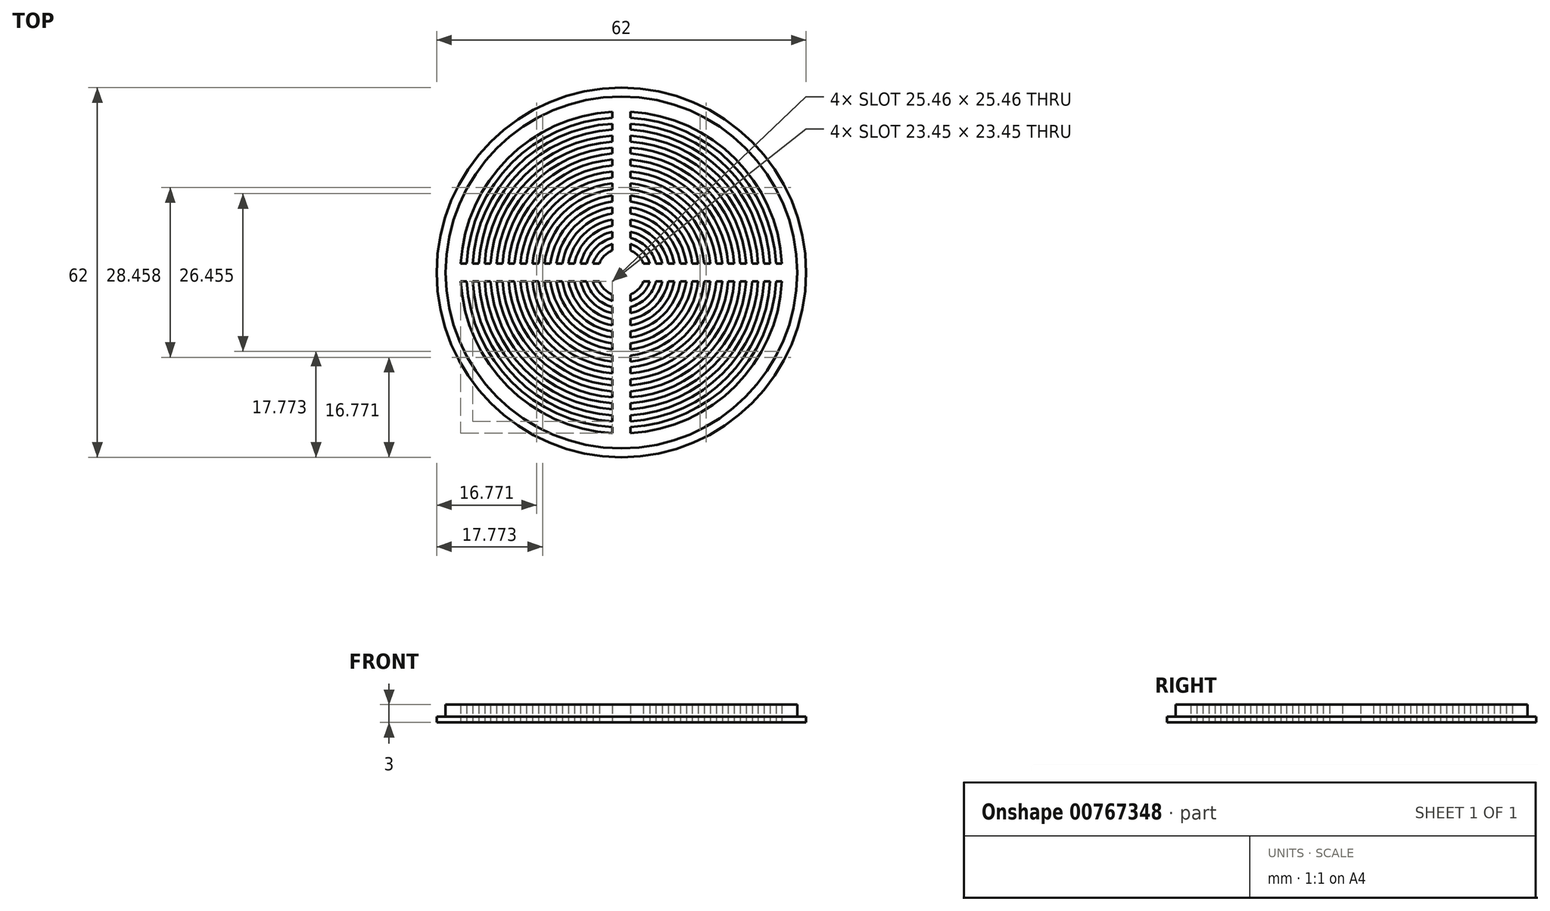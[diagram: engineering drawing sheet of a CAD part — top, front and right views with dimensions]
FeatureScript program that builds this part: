
annotation { "Feature Type Name" : "Feature", "Feature Type Description" : "" }
export const myFeature = defineFeature(function(context is Context, id is Id, definition is map)
    precondition{}
    {
        {
            var Q0;
            Q0=qCreatedBy(makeId("Top.planeOp"),FACE);
            var sketch = newSketch(context, id + "F0", { "sketchPlane" : qUnion([Q0])});
            skPoint(sketch, "E0.middle", {"position": v(0, 0) * mm});
            skCircle(sketch, "E1", {"center": v(0, 0) * mm, "radius": 29.5 * mm});
            skCircle(sketch, "E2", {"center": v(0, 0) * mm, "radius": 27 * mm});
            skCircle(sketch, "E3", {"center": v(0, 0) * mm, "radius": 26 * mm});
            skCircle(sketch, "E4", {"center": v(0, 0) * mm, "radius": 25 * mm});
            skCircle(sketch, "E5", {"center": v(0, 0) * mm, "radius": 24 * mm});
            skCircle(sketch, "E6", {"center": v(0, 0) * mm, "radius": 23 * mm});
            skCircle(sketch, "E7", {"center": v(0, 0) * mm, "radius": 22 * mm});
            skCircle(sketch, "E8", {"center": v(0, 0) * mm, "radius": 21 * mm});
            skCircle(sketch, "E9", {"center": v(0, 0) * mm, "radius": 20 * mm});
            skCircle(sketch, "E10", {"center": v(0, 0) * mm, "radius": 19 * mm});
            skCircle(sketch, "E11", {"center": v(0, 0) * mm, "radius": 18 * mm});
            skCircle(sketch, "E12", {"center": v(0, 0) * mm, "radius": 17 * mm});
            skCircle(sketch, "E13", {"center": v(0, 0) * mm, "radius": 16 * mm});
            skCircle(sketch, "E14", {"center": v(0, 0) * mm, "radius": 15 * mm});
            skCircle(sketch, "E15", {"center": v(0, 0) * mm, "radius": 14 * mm});
            skCircle(sketch, "E16", {"center": v(0, 0) * mm, "radius": 13 * mm});
            skCircle(sketch, "E17", {"center": v(0, 0) * mm, "radius": 12 * mm});
            skCircle(sketch, "E18", {"center": v(0, 0) * mm, "radius": 11 * mm});
            skCircle(sketch, "E19", {"center": v(0, 0) * mm, "radius": 10 * mm});
            skCircle(sketch, "E20", {"center": v(0, 0) * mm, "radius": 9 * mm});
            skCircle(sketch, "E21", {"center": v(0, 0) * mm, "radius": 8 * mm});
            skCircle(sketch, "E22", {"center": v(0, 0) * mm, "radius": 7 * mm});
            skCircle(sketch, "E23", {"center": v(0, 0) * mm, "radius": 6 * mm});
            skCircle(sketch, "E24", {"center": v(0, 0) * mm, "radius": 5 * mm});
            skCircle(sketch, "E25", {"center": v(0, 0) * mm, "radius": 4 * mm});
            skCircle(sketch, "E26", {"center": v(0, 0) * mm, "radius": 3 * mm});
            skCircle(sketch, "E27", {"center": v(0, 0) * mm, "radius": 2 * mm});
            skCircle(sketch, "E28", {"center": v(0, 0) * mm, "radius": 1 * mm});
            skLineSegment(sketch, "E29.bottom", {"start": v(-1.5, 32.48) * mm, "end": v(1.5, 32.48) * mm});
            skLineSegment(sketch, "E29.top", {"start": v(-1.5, -32.48) * mm, "end": v(1.5, -32.48) * mm});
            skLineSegment(sketch, "E29.left", {"start": v(-1.5, 32.48) * mm, "end": v(-1.5, -32.48) * mm});
            skLineSegment(sketch, "E29.right", {"start": v(1.5, 32.48) * mm, "end": v(1.5, -32.48) * mm});
            skLineSegment(sketch, "E30.bottom", {"start": v(36.63, -1.5) * mm, "end": v(-36.63, -1.5) * mm});
            skLineSegment(sketch, "E30.top", {"start": v(36.63, 1.5) * mm, "end": v(-36.63, 1.5) * mm});
            skLineSegment(sketch, "E30.left", {"start": v(36.63, -1.5) * mm, "end": v(36.63, 1.5) * mm});
            skLineSegment(sketch, "E30.right", {"start": v(-36.63, -1.5) * mm, "end": v(-36.63, 1.5) * mm});
            skCircle(sketch, "E31", {"center": v(0, 0) * mm, "radius": 31 * mm});
            skSolve(sketch);
        }
        {
            var Q0;
            {var subQ0=sQuery(id+"F0.wireOp",EDGE,"E30.top");var subQ1=sQuery(id+"F0.wireOp",EDGE,"E10");var subQ2=makeQuery(id+"F0.imprint","INTERSECT",VERTEX,{"disambiguationData":[OD(1.0)],"derivedFrom":[subQ1,subQ0]});Q0=makeQuery(id+"F0.imprint","IMPRINT",FACE,{"disambiguationData":[TD([[makeQuery(id+"F0.imprint","IMPRINT",EDGE,{"disambiguationData":[TD([[subQ2,-1.0]])],"derivedFrom":subQ1}),1.0]])]});}
            var Q1;
            {var subQ0=sQuery(id+"F0.wireOp",EDGE,"E30.top");var subQ1=sQuery(id+"F0.wireOp",EDGE,"E16");var subQ2=makeQuery(id+"F0.imprint","INTERSECT",VERTEX,{"disambiguationData":[OD(1.0)],"derivedFrom":[subQ1,subQ0]});Q1=makeQuery(id+"F0.imprint","IMPRINT",FACE,{"disambiguationData":[TD([[makeQuery(id+"F0.imprint","IMPRINT",EDGE,{"disambiguationData":[TD([[subQ2,-1.0]])],"derivedFrom":subQ1}),1.0]])]});}
            var Q2;
            {var subQ0=sQuery(id+"F0.wireOp",EDGE,"E30.top");var subQ1=sQuery(id+"F0.wireOp",EDGE,"E1");var subQ2=makeQuery(id+"F0.imprint","INTERSECT",VERTEX,{"disambiguationData":[OD(0.0)],"derivedFrom":[subQ1,subQ0]});Q2=makeQuery(id+"F0.imprint","IMPRINT",FACE,{"disambiguationData":[TD([[makeQuery(id+"F0.imprint","IMPRINT",EDGE,{"disambiguationData":[TD([[subQ2,1.0]])],"derivedFrom":subQ1}),1.0]])]});}
            var Q3;
            {var subQ0=sQuery(id+"F0.wireOp",EDGE,"E30.top");var subQ1=sQuery(id+"F0.wireOp",EDGE,"E3");var subQ2=makeQuery(id+"F0.imprint","INTERSECT",VERTEX,{"disambiguationData":[OD(0.0)],"derivedFrom":[subQ1,subQ0]});Q3=makeQuery(id+"F0.imprint","IMPRINT",FACE,{"disambiguationData":[TD([[makeQuery(id+"F0.imprint","IMPRINT",EDGE,{"disambiguationData":[TD([[subQ2,1.0]])],"derivedFrom":subQ1}),1.0]])]});}
            var Q4;
            {var subQ0=sQuery(id+"F0.wireOp",EDGE,"E30.top");var subQ1=sQuery(id+"F0.wireOp",EDGE,"E11");var subQ2=makeQuery(id+"F0.imprint","INTERSECT",VERTEX,{"disambiguationData":[OD(0.0)],"derivedFrom":[subQ1,subQ0]});Q4=makeQuery(id+"F0.imprint","IMPRINT",FACE,{"disambiguationData":[TD([[makeQuery(id+"F0.imprint","IMPRINT",EDGE,{"disambiguationData":[TD([[subQ2,1.0]])],"derivedFrom":subQ1}),1.0]])]});}
            var Q5;
            {var subQ0=sQuery(id+"F0.wireOp",EDGE,"E30.top");var subQ1=sQuery(id+"F0.wireOp",EDGE,"E8");var subQ2=makeQuery(id+"F0.imprint","INTERSECT",VERTEX,{"disambiguationData":[OD(1.0)],"derivedFrom":[subQ1,subQ0]});Q5=makeQuery(id+"F0.imprint","IMPRINT",FACE,{"disambiguationData":[TD([[makeQuery(id+"F0.imprint","IMPRINT",EDGE,{"disambiguationData":[TD([[subQ2,-1.0]])],"derivedFrom":subQ1}),1.0]])]});}
            var Q6;
            {var subQ0=sQuery(id+"F0.wireOp",EDGE,"E30.top");var subQ1=sQuery(id+"F0.wireOp",EDGE,"E2");var subQ2=makeQuery(id+"F0.imprint","INTERSECT",VERTEX,{"disambiguationData":[OD(1.0)],"derivedFrom":[subQ1,subQ0]});Q6=makeQuery(id+"F0.imprint","IMPRINT",FACE,{"disambiguationData":[TD([[makeQuery(id+"F0.imprint","IMPRINT",EDGE,{"disambiguationData":[TD([[subQ2,-1.0]])],"derivedFrom":subQ1}),1.0]])]});}
            var Q7;
            {var subQ3=sQuery(id+"F0.wireOp",EDGE,"E30.top");var subQ6=sQuery(id+"F0.wireOp",EDGE,"E26");var subQ7=makeQuery(id+"F0.imprint","INTERSECT",VERTEX,{"disambiguationData":[OD(1.0)],"derivedFrom":[subQ6,subQ3]});Q7=makeQuery(id+"F0.imprint","IMPRINT",FACE,{"disambiguationData":[TD([[makeQuery(id+"F0.imprint","IMPRINT",EDGE,{"disambiguationData":[TD([[subQ7,-1.0]])],"derivedFrom":subQ6}),1.0]])]});}
            var Q8;
            {var subQ0=sQuery(id+"F0.wireOp",EDGE,"E30.top");var subQ1=sQuery(id+"F0.wireOp",EDGE,"E4");var subQ2=makeQuery(id+"F0.imprint","INTERSECT",VERTEX,{"disambiguationData":[OD(1.0)],"derivedFrom":[subQ1,subQ0]});Q8=makeQuery(id+"F0.imprint","IMPRINT",FACE,{"disambiguationData":[TD([[makeQuery(id+"F0.imprint","IMPRINT",EDGE,{"disambiguationData":[TD([[subQ2,-1.0]])],"derivedFrom":subQ1}),1.0]])]});}
            var Q9;
            {var subQ0=sQuery(id+"F0.wireOp",EDGE,"E30.top");var subQ1=sQuery(id+"F0.wireOp",EDGE,"E6");var subQ2=makeQuery(id+"F0.imprint","INTERSECT",VERTEX,{"disambiguationData":[OD(1.0)],"derivedFrom":[subQ1,subQ0]});Q9=makeQuery(id+"F0.imprint","IMPRINT",FACE,{"disambiguationData":[TD([[makeQuery(id+"F0.imprint","IMPRINT",EDGE,{"disambiguationData":[TD([[subQ2,-1.0]])],"derivedFrom":subQ1}),1.0]])]});}
            var Q10;
            {var subQ0=sQuery(id+"F0.wireOp",EDGE,"E30.top");var subQ1=sQuery(id+"F0.wireOp",EDGE,"E24");var subQ2=makeQuery(id+"F0.imprint","INTERSECT",VERTEX,{"disambiguationData":[OD(0.0)],"derivedFrom":[subQ1,subQ0]});Q10=makeQuery(id+"F0.imprint","IMPRINT",FACE,{"disambiguationData":[TD([[makeQuery(id+"F0.imprint","IMPRINT",EDGE,{"disambiguationData":[TD([[subQ2,1.0]])],"derivedFrom":subQ1}),1.0]])]});}
            var Q11;
            {var subQ0=sQuery(id+"F0.wireOp",EDGE,"E30.top");var subQ1=sQuery(id+"F0.wireOp",EDGE,"E20");var subQ2=makeQuery(id+"F0.imprint","INTERSECT",VERTEX,{"disambiguationData":[OD(1.0)],"derivedFrom":[subQ1,subQ0]});Q11=makeQuery(id+"F0.imprint","IMPRINT",FACE,{"disambiguationData":[TD([[makeQuery(id+"F0.imprint","IMPRINT",EDGE,{"disambiguationData":[TD([[subQ2,-1.0]])],"derivedFrom":subQ1}),1.0]])]});}
            var Q12;
            {var subQ0=sQuery(id+"F0.wireOp",EDGE,"E30.top");var subQ1=sQuery(id+"F0.wireOp",EDGE,"E14");var subQ2=makeQuery(id+"F0.imprint","INTERSECT",VERTEX,{"disambiguationData":[OD(1.0)],"derivedFrom":[subQ1,subQ0]});Q12=makeQuery(id+"F0.imprint","IMPRINT",FACE,{"disambiguationData":[TD([[makeQuery(id+"F0.imprint","IMPRINT",EDGE,{"disambiguationData":[TD([[subQ2,-1.0]])],"derivedFrom":subQ1}),1.0]])]});}
            var Q13;
            {var subQ0=sQuery(id+"F0.wireOp",EDGE,"E30.top");var subQ1=sQuery(id+"F0.wireOp",EDGE,"E12");var subQ2=makeQuery(id+"F0.imprint","INTERSECT",VERTEX,{"disambiguationData":[OD(1.0)],"derivedFrom":[subQ1,subQ0]});Q13=makeQuery(id+"F0.imprint","IMPRINT",FACE,{"disambiguationData":[TD([[makeQuery(id+"F0.imprint","IMPRINT",EDGE,{"disambiguationData":[TD([[subQ2,-1.0]])],"derivedFrom":subQ1}),1.0]])]});}
            var Q14;
            {var subQ0=sQuery(id+"F0.wireOp",EDGE,"E30.top");var subQ1=sQuery(id+"F0.wireOp",EDGE,"E22");var subQ2=makeQuery(id+"F0.imprint","INTERSECT",VERTEX,{"disambiguationData":[OD(1.0)],"derivedFrom":[subQ1,subQ0]});Q14=makeQuery(id+"F0.imprint","IMPRINT",FACE,{"disambiguationData":[TD([[makeQuery(id+"F0.imprint","IMPRINT",EDGE,{"disambiguationData":[TD([[subQ2,-1.0]])],"derivedFrom":subQ1}),1.0]])]});}
            var Q15;
            {var subQ3=sQuery(id+"F0.wireOp",EDGE,"E30.top");var subQ8=sQuery(id+"F0.wireOp",EDGE,"E26");var subQ9=makeQuery(id+"F0.imprint","INTERSECT",VERTEX,{"disambiguationData":[OD(0.0)],"derivedFrom":[subQ8,subQ3]});Q15=makeQuery(id+"F0.imprint","IMPRINT",FACE,{"disambiguationData":[TD([[makeQuery(id+"F0.imprint","IMPRINT",EDGE,{"disambiguationData":[TD([[subQ9,1.0]])],"derivedFrom":subQ8}),1.0]])]});}
            var Q16;
            {var subQ0=sQuery(id+"F0.wireOp",EDGE,"E30.top");var subQ1=sQuery(id+"F0.wireOp",EDGE,"E24");var subQ2=makeQuery(id+"F0.imprint","INTERSECT",VERTEX,{"disambiguationData":[OD(1.0)],"derivedFrom":[subQ1,subQ0]});Q16=makeQuery(id+"F0.imprint","IMPRINT",FACE,{"disambiguationData":[TD([[makeQuery(id+"F0.imprint","IMPRINT",EDGE,{"disambiguationData":[TD([[subQ2,-1.0]])],"derivedFrom":subQ1}),1.0]])]});}
            var Q17;
            {var subQ0=sQuery(id+"F0.wireOp",EDGE,"E30.top");var subQ1=sQuery(id+"F0.wireOp",EDGE,"E18");var subQ2=makeQuery(id+"F0.imprint","INTERSECT",VERTEX,{"disambiguationData":[OD(1.0)],"derivedFrom":[subQ1,subQ0]});Q17=makeQuery(id+"F0.imprint","IMPRINT",FACE,{"disambiguationData":[TD([[makeQuery(id+"F0.imprint","IMPRINT",EDGE,{"disambiguationData":[TD([[subQ2,-1.0]])],"derivedFrom":subQ1}),1.0]])]});}
            var Q18;
            {var subQ0=sQuery(id+"F0.wireOp",EDGE,"E30.top");var subQ1=sQuery(id+"F0.wireOp",EDGE,"E13");var subQ2=makeQuery(id+"F0.imprint","INTERSECT",VERTEX,{"disambiguationData":[OD(0.0)],"derivedFrom":[subQ1,subQ0]});Q18=makeQuery(id+"F0.imprint","IMPRINT",FACE,{"disambiguationData":[TD([[makeQuery(id+"F0.imprint","IMPRINT",EDGE,{"disambiguationData":[TD([[subQ2,1.0]])],"derivedFrom":subQ1}),1.0]])]});}
            var Q19;
            {var subQ0=sQuery(id+"F0.wireOp",EDGE,"E30.top");var subQ1=sQuery(id+"F0.wireOp",EDGE,"E25");var subQ2=makeQuery(id+"F0.imprint","INTERSECT",VERTEX,{"disambiguationData":[OD(0.0)],"derivedFrom":[subQ1,subQ0]});Q19=makeQuery(id+"F0.imprint","IMPRINT",FACE,{"disambiguationData":[TD([[makeQuery(id+"F0.imprint","IMPRINT",EDGE,{"disambiguationData":[TD([[subQ2,1.0]])],"derivedFrom":subQ1}),1.0]])]});}
            var Q20;
            {var subQ0=sQuery(id+"F0.wireOp",EDGE,"E30.top");var subQ1=sQuery(id+"F0.wireOp",EDGE,"E20");var subQ2=makeQuery(id+"F0.imprint","INTERSECT",VERTEX,{"disambiguationData":[OD(0.0)],"derivedFrom":[subQ1,subQ0]});Q20=makeQuery(id+"F0.imprint","IMPRINT",FACE,{"disambiguationData":[TD([[makeQuery(id+"F0.imprint","IMPRINT",EDGE,{"disambiguationData":[TD([[subQ2,1.0]])],"derivedFrom":subQ1}),1.0]])]});}
            var Q21;
            {var subQ0=sQuery(id+"F0.wireOp",EDGE,"E30.top");var subQ1=sQuery(id+"F0.wireOp",EDGE,"E17");var subQ2=makeQuery(id+"F0.imprint","INTERSECT",VERTEX,{"disambiguationData":[OD(0.0)],"derivedFrom":[subQ1,subQ0]});Q21=makeQuery(id+"F0.imprint","IMPRINT",FACE,{"disambiguationData":[TD([[makeQuery(id+"F0.imprint","IMPRINT",EDGE,{"disambiguationData":[TD([[subQ2,1.0]])],"derivedFrom":subQ1}),1.0]])]});}
            var Q22;
            {var subQ0=sQuery(id+"F0.wireOp",EDGE,"E30.top");var subQ1=sQuery(id+"F0.wireOp",EDGE,"E10");var subQ2=makeQuery(id+"F0.imprint","INTERSECT",VERTEX,{"disambiguationData":[OD(0.0)],"derivedFrom":[subQ1,subQ0]});Q22=makeQuery(id+"F0.imprint","IMPRINT",FACE,{"disambiguationData":[TD([[makeQuery(id+"F0.imprint","IMPRINT",EDGE,{"disambiguationData":[TD([[subQ2,1.0]])],"derivedFrom":subQ1}),1.0]])]});}
            var Q23;
            {var subQ0=sQuery(id+"F0.wireOp",EDGE,"E30.top");var subQ1=sQuery(id+"F0.wireOp",EDGE,"E22");var subQ2=makeQuery(id+"F0.imprint","INTERSECT",VERTEX,{"disambiguationData":[OD(0.0)],"derivedFrom":[subQ1,subQ0]});Q23=makeQuery(id+"F0.imprint","IMPRINT",FACE,{"disambiguationData":[TD([[makeQuery(id+"F0.imprint","IMPRINT",EDGE,{"disambiguationData":[TD([[subQ2,1.0]])],"derivedFrom":subQ1}),1.0]])]});}
            var Q24;
            {var subQ0=sQuery(id+"F0.wireOp",EDGE,"E30.top");var subQ1=sQuery(id+"F0.wireOp",EDGE,"E12");var subQ2=makeQuery(id+"F0.imprint","INTERSECT",VERTEX,{"disambiguationData":[OD(0.0)],"derivedFrom":[subQ1,subQ0]});Q24=makeQuery(id+"F0.imprint","IMPRINT",FACE,{"disambiguationData":[TD([[makeQuery(id+"F0.imprint","IMPRINT",EDGE,{"disambiguationData":[TD([[subQ2,1.0]])],"derivedFrom":subQ1}),1.0]])]});}
            var Q25;
            {var subQ0=sQuery(id+"F0.wireOp",EDGE,"E30.top");var subQ1=sQuery(id+"F0.wireOp",EDGE,"E23");var subQ2=makeQuery(id+"F0.imprint","INTERSECT",VERTEX,{"disambiguationData":[OD(0.0)],"derivedFrom":[subQ1,subQ0]});Q25=makeQuery(id+"F0.imprint","IMPRINT",FACE,{"disambiguationData":[TD([[makeQuery(id+"F0.imprint","IMPRINT",EDGE,{"disambiguationData":[TD([[subQ2,1.0]])],"derivedFrom":subQ1}),1.0]])]});}
            var Q26;
            {var subQ0=sQuery(id+"F0.wireOp",EDGE,"E30.top");var subQ1=sQuery(id+"F0.wireOp",EDGE,"E19");var subQ2=makeQuery(id+"F0.imprint","INTERSECT",VERTEX,{"disambiguationData":[OD(0.0)],"derivedFrom":[subQ1,subQ0]});Q26=makeQuery(id+"F0.imprint","IMPRINT",FACE,{"disambiguationData":[TD([[makeQuery(id+"F0.imprint","IMPRINT",EDGE,{"disambiguationData":[TD([[subQ2,1.0]])],"derivedFrom":subQ1}),1.0]])]});}
            var Q27;
            {var subQ0=sQuery(id+"F0.wireOp",EDGE,"E30.top");var subQ1=sQuery(id+"F0.wireOp",EDGE,"E21");var subQ2=makeQuery(id+"F0.imprint","INTERSECT",VERTEX,{"disambiguationData":[OD(0.0)],"derivedFrom":[subQ1,subQ0]});Q27=makeQuery(id+"F0.imprint","IMPRINT",FACE,{"disambiguationData":[TD([[makeQuery(id+"F0.imprint","IMPRINT",EDGE,{"disambiguationData":[TD([[subQ2,1.0]])],"derivedFrom":subQ1}),1.0]])]});}
            var Q28;
            {var subQ0=sQuery(id+"F0.wireOp",EDGE,"E30.top");var subQ1=sQuery(id+"F0.wireOp",EDGE,"E7");var subQ2=makeQuery(id+"F0.imprint","INTERSECT",VERTEX,{"disambiguationData":[OD(0.0)],"derivedFrom":[subQ1,subQ0]});Q28=makeQuery(id+"F0.imprint","IMPRINT",FACE,{"disambiguationData":[TD([[makeQuery(id+"F0.imprint","IMPRINT",EDGE,{"disambiguationData":[TD([[subQ2,1.0]])],"derivedFrom":subQ1}),1.0]])]});}
            var Q29;
            {var subQ0=sQuery(id+"F0.wireOp",EDGE,"E30.top");var subQ1=sQuery(id+"F0.wireOp",EDGE,"E9");var subQ2=makeQuery(id+"F0.imprint","INTERSECT",VERTEX,{"disambiguationData":[OD(0.0)],"derivedFrom":[subQ1,subQ0]});Q29=makeQuery(id+"F0.imprint","IMPRINT",FACE,{"disambiguationData":[TD([[makeQuery(id+"F0.imprint","IMPRINT",EDGE,{"disambiguationData":[TD([[subQ2,1.0]])],"derivedFrom":subQ1}),1.0]])]});}
            var Q30;
            {var subQ0=sQuery(id+"F0.wireOp",EDGE,"E30.top");var subQ1=sQuery(id+"F0.wireOp",EDGE,"E18");var subQ2=makeQuery(id+"F0.imprint","INTERSECT",VERTEX,{"disambiguationData":[OD(0.0)],"derivedFrom":[subQ1,subQ0]});Q30=makeQuery(id+"F0.imprint","IMPRINT",FACE,{"disambiguationData":[TD([[makeQuery(id+"F0.imprint","IMPRINT",EDGE,{"disambiguationData":[TD([[subQ2,1.0]])],"derivedFrom":subQ1}),1.0]])]});}
            var Q31;
            {var subQ0=sQuery(id+"F0.wireOp",EDGE,"E30.top");var subQ1=sQuery(id+"F0.wireOp",EDGE,"E15");var subQ2=makeQuery(id+"F0.imprint","INTERSECT",VERTEX,{"disambiguationData":[OD(0.0)],"derivedFrom":[subQ1,subQ0]});Q31=makeQuery(id+"F0.imprint","IMPRINT",FACE,{"disambiguationData":[TD([[makeQuery(id+"F0.imprint","IMPRINT",EDGE,{"disambiguationData":[TD([[subQ2,1.0]])],"derivedFrom":subQ1}),1.0]])]});}
            var Q32;
            {var subQ0=sQuery(id+"F0.wireOp",EDGE,"E30.top");var subQ1=sQuery(id+"F0.wireOp",EDGE,"E5");var subQ2=makeQuery(id+"F0.imprint","INTERSECT",VERTEX,{"disambiguationData":[OD(0.0)],"derivedFrom":[subQ1,subQ0]});Q32=makeQuery(id+"F0.imprint","IMPRINT",FACE,{"disambiguationData":[TD([[makeQuery(id+"F0.imprint","IMPRINT",EDGE,{"disambiguationData":[TD([[subQ2,1.0]])],"derivedFrom":subQ1}),1.0]])]});}
            var Q33;
            {var subQ0=sQuery(id+"F0.wireOp",EDGE,"E30.top");var subQ1=sQuery(id+"F0.wireOp",EDGE,"E8");var subQ2=makeQuery(id+"F0.imprint","INTERSECT",VERTEX,{"disambiguationData":[OD(0.0)],"derivedFrom":[subQ1,subQ0]});Q33=makeQuery(id+"F0.imprint","IMPRINT",FACE,{"disambiguationData":[TD([[makeQuery(id+"F0.imprint","IMPRINT",EDGE,{"disambiguationData":[TD([[subQ2,1.0]])],"derivedFrom":subQ1}),1.0]])]});}
            var Q34;
            {var subQ0=sQuery(id+"F0.wireOp",EDGE,"E30.top");var subQ1=sQuery(id+"F0.wireOp",EDGE,"E4");var subQ2=makeQuery(id+"F0.imprint","INTERSECT",VERTEX,{"disambiguationData":[OD(0.0)],"derivedFrom":[subQ1,subQ0]});Q34=makeQuery(id+"F0.imprint","IMPRINT",FACE,{"disambiguationData":[TD([[makeQuery(id+"F0.imprint","IMPRINT",EDGE,{"disambiguationData":[TD([[subQ2,1.0]])],"derivedFrom":subQ1}),1.0]])]});}
            var Q35;
            {var subQ0=sQuery(id+"F0.wireOp",EDGE,"E30.top");var subQ1=sQuery(id+"F0.wireOp",EDGE,"E6");var subQ2=makeQuery(id+"F0.imprint","INTERSECT",VERTEX,{"disambiguationData":[OD(0.0)],"derivedFrom":[subQ1,subQ0]});Q35=makeQuery(id+"F0.imprint","IMPRINT",FACE,{"disambiguationData":[TD([[makeQuery(id+"F0.imprint","IMPRINT",EDGE,{"disambiguationData":[TD([[subQ2,1.0]])],"derivedFrom":subQ1}),1.0]])]});}
            var Q36;
            {var subQ0=sQuery(id+"F0.wireOp",EDGE,"E30.top");var subQ1=sQuery(id+"F0.wireOp",EDGE,"E2");var subQ2=makeQuery(id+"F0.imprint","INTERSECT",VERTEX,{"disambiguationData":[OD(0.0)],"derivedFrom":[subQ1,subQ0]});Q36=makeQuery(id+"F0.imprint","IMPRINT",FACE,{"disambiguationData":[TD([[makeQuery(id+"F0.imprint","IMPRINT",EDGE,{"disambiguationData":[TD([[subQ2,1.0]])],"derivedFrom":subQ1}),1.0]])]});}
            var Q37;
            {var subQ0=sQuery(id+"F0.wireOp",EDGE,"E30.top");var subQ1=sQuery(id+"F0.wireOp",EDGE,"E14");var subQ2=makeQuery(id+"F0.imprint","INTERSECT",VERTEX,{"disambiguationData":[OD(0.0)],"derivedFrom":[subQ1,subQ0]});Q37=makeQuery(id+"F0.imprint","IMPRINT",FACE,{"disambiguationData":[TD([[makeQuery(id+"F0.imprint","IMPRINT",EDGE,{"disambiguationData":[TD([[subQ2,1.0]])],"derivedFrom":subQ1}),1.0]])]});}
            var Q38;
            {var subQ0=sQuery(id+"F0.wireOp",EDGE,"E30.top");var subQ1=sQuery(id+"F0.wireOp",EDGE,"E16");var subQ2=makeQuery(id+"F0.imprint","INTERSECT",VERTEX,{"disambiguationData":[OD(0.0)],"derivedFrom":[subQ1,subQ0]});Q38=makeQuery(id+"F0.imprint","IMPRINT",FACE,{"disambiguationData":[TD([[makeQuery(id+"F0.imprint","IMPRINT",EDGE,{"disambiguationData":[TD([[subQ2,1.0]])],"derivedFrom":subQ1}),1.0]])]});}
            var Q39;
            {var subQ0=sQuery(id+"F0.wireOp",EDGE,"E30.top");var subQ1=sQuery(id+"F0.wireOp",EDGE,"E9");var subQ2=makeQuery(id+"F0.imprint","INTERSECT",VERTEX,{"disambiguationData":[OD(1.0)],"derivedFrom":[subQ1,subQ0]});Q39=makeQuery(id+"F0.imprint","IMPRINT",FACE,{"disambiguationData":[TD([[makeQuery(id+"F0.imprint","IMPRINT",EDGE,{"disambiguationData":[TD([[subQ2,-1.0]])],"derivedFrom":subQ1}),1.0]])]});}
            var Q40;
            {var subQ0=sQuery(id+"F0.wireOp",EDGE,"E30.top");var subQ1=sQuery(id+"F0.wireOp",EDGE,"E7");var subQ2=makeQuery(id+"F0.imprint","INTERSECT",VERTEX,{"disambiguationData":[OD(1.0)],"derivedFrom":[subQ1,subQ0]});Q40=makeQuery(id+"F0.imprint","IMPRINT",FACE,{"disambiguationData":[TD([[makeQuery(id+"F0.imprint","IMPRINT",EDGE,{"disambiguationData":[TD([[subQ2,-1.0]])],"derivedFrom":subQ1}),1.0]])]});}
            var Q41;
            {var subQ0=sQuery(id+"F0.wireOp",EDGE,"E30.top");var subQ1=sQuery(id+"F0.wireOp",EDGE,"E5");var subQ2=makeQuery(id+"F0.imprint","INTERSECT",VERTEX,{"disambiguationData":[OD(1.0)],"derivedFrom":[subQ1,subQ0]});Q41=makeQuery(id+"F0.imprint","IMPRINT",FACE,{"disambiguationData":[TD([[makeQuery(id+"F0.imprint","IMPRINT",EDGE,{"disambiguationData":[TD([[subQ2,-1.0]])],"derivedFrom":subQ1}),1.0]])]});}
            var Q42;
            {var subQ0=sQuery(id+"F0.wireOp",EDGE,"E30.top");var subQ1=sQuery(id+"F0.wireOp",EDGE,"E3");var subQ2=makeQuery(id+"F0.imprint","INTERSECT",VERTEX,{"disambiguationData":[OD(1.0)],"derivedFrom":[subQ1,subQ0]});Q42=makeQuery(id+"F0.imprint","IMPRINT",FACE,{"disambiguationData":[TD([[makeQuery(id+"F0.imprint","IMPRINT",EDGE,{"disambiguationData":[TD([[subQ2,-1.0]])],"derivedFrom":subQ1}),1.0]])]});}
            var Q43;
            {var subQ0=sQuery(id+"F0.wireOp",EDGE,"E30.top");var subQ1=sQuery(id+"F0.wireOp",EDGE,"E17");var subQ2=makeQuery(id+"F0.imprint","INTERSECT",VERTEX,{"disambiguationData":[OD(1.0)],"derivedFrom":[subQ1,subQ0]});Q43=makeQuery(id+"F0.imprint","IMPRINT",FACE,{"disambiguationData":[TD([[makeQuery(id+"F0.imprint","IMPRINT",EDGE,{"disambiguationData":[TD([[subQ2,-1.0]])],"derivedFrom":subQ1}),1.0]])]});}
            var Q44;
            {var subQ0=sQuery(id+"F0.wireOp",EDGE,"E30.top");var subQ1=sQuery(id+"F0.wireOp",EDGE,"E15");var subQ2=makeQuery(id+"F0.imprint","INTERSECT",VERTEX,{"disambiguationData":[OD(1.0)],"derivedFrom":[subQ1,subQ0]});Q44=makeQuery(id+"F0.imprint","IMPRINT",FACE,{"disambiguationData":[TD([[makeQuery(id+"F0.imprint","IMPRINT",EDGE,{"disambiguationData":[TD([[subQ2,-1.0]])],"derivedFrom":subQ1}),1.0]])]});}
            var Q45;
            {var subQ0=sQuery(id+"F0.wireOp",EDGE,"E30.top");var subQ1=sQuery(id+"F0.wireOp",EDGE,"E13");var subQ2=makeQuery(id+"F0.imprint","INTERSECT",VERTEX,{"disambiguationData":[OD(1.0)],"derivedFrom":[subQ1,subQ0]});Q45=makeQuery(id+"F0.imprint","IMPRINT",FACE,{"disambiguationData":[TD([[makeQuery(id+"F0.imprint","IMPRINT",EDGE,{"disambiguationData":[TD([[subQ2,-1.0]])],"derivedFrom":subQ1}),1.0]])]});}
            var Q46;
            {var subQ0=sQuery(id+"F0.wireOp",EDGE,"E30.top");var subQ1=sQuery(id+"F0.wireOp",EDGE,"E11");var subQ2=makeQuery(id+"F0.imprint","INTERSECT",VERTEX,{"disambiguationData":[OD(1.0)],"derivedFrom":[subQ1,subQ0]});Q46=makeQuery(id+"F0.imprint","IMPRINT",FACE,{"disambiguationData":[TD([[makeQuery(id+"F0.imprint","IMPRINT",EDGE,{"disambiguationData":[TD([[subQ2,-1.0]])],"derivedFrom":subQ1}),1.0]])]});}
            var Q47;
            {var subQ0=sQuery(id+"F0.wireOp",EDGE,"E30.top");var subQ1=sQuery(id+"F0.wireOp",EDGE,"E25");var subQ2=makeQuery(id+"F0.imprint","INTERSECT",VERTEX,{"disambiguationData":[OD(1.0)],"derivedFrom":[subQ1,subQ0]});Q47=makeQuery(id+"F0.imprint","IMPRINT",FACE,{"disambiguationData":[TD([[makeQuery(id+"F0.imprint","IMPRINT",EDGE,{"disambiguationData":[TD([[subQ2,-1.0]])],"derivedFrom":subQ1}),1.0]])]});}
            var Q48;
            {var subQ0=sQuery(id+"F0.wireOp",EDGE,"E30.top");var subQ1=sQuery(id+"F0.wireOp",EDGE,"E23");var subQ2=makeQuery(id+"F0.imprint","INTERSECT",VERTEX,{"disambiguationData":[OD(1.0)],"derivedFrom":[subQ1,subQ0]});Q48=makeQuery(id+"F0.imprint","IMPRINT",FACE,{"disambiguationData":[TD([[makeQuery(id+"F0.imprint","IMPRINT",EDGE,{"disambiguationData":[TD([[subQ2,-1.0]])],"derivedFrom":subQ1}),1.0]])]});}
            var Q49;
            {var subQ0=sQuery(id+"F0.wireOp",EDGE,"E30.top");var subQ1=sQuery(id+"F0.wireOp",EDGE,"E21");var subQ2=makeQuery(id+"F0.imprint","INTERSECT",VERTEX,{"disambiguationData":[OD(1.0)],"derivedFrom":[subQ1,subQ0]});Q49=makeQuery(id+"F0.imprint","IMPRINT",FACE,{"disambiguationData":[TD([[makeQuery(id+"F0.imprint","IMPRINT",EDGE,{"disambiguationData":[TD([[subQ2,-1.0]])],"derivedFrom":subQ1}),1.0]])]});}
            var Q50;
            {var subQ0=sQuery(id+"F0.wireOp",EDGE,"E30.top");var subQ1=sQuery(id+"F0.wireOp",EDGE,"E19");var subQ2=makeQuery(id+"F0.imprint","INTERSECT",VERTEX,{"disambiguationData":[OD(1.0)],"derivedFrom":[subQ1,subQ0]});Q50=makeQuery(id+"F0.imprint","IMPRINT",FACE,{"disambiguationData":[TD([[makeQuery(id+"F0.imprint","IMPRINT",EDGE,{"disambiguationData":[TD([[subQ2,-1.0]])],"derivedFrom":subQ1}),1.0]])]});}
            var Q51;
            {var subQ0=sQuery(id+"F0.wireOp",EDGE,"E30.top");var subQ1=sQuery(id+"F0.wireOp",EDGE,"E1");var subQ2=makeQuery(id+"F0.imprint","INTERSECT",VERTEX,{"disambiguationData":[OD(1.0)],"derivedFrom":[subQ1,subQ0]});Q51=makeQuery(id+"F0.imprint","IMPRINT",FACE,{"disambiguationData":[TD([[makeQuery(id+"F0.imprint","IMPRINT",EDGE,{"disambiguationData":[TD([[subQ2,-1.0]])],"derivedFrom":subQ1}),1.0]])]});}
            var Q52;
            Q52=makeQuery(id+"F0.imprint","IMPRINT",FACE,{"disambiguationData":[TD([[makeQuery(id+"F0.imprint","IMPRINT",EDGE,{"derivedFrom":sQuery(id+"F0.wireOp",EDGE,"E28")}),-1.0]])]});
            var Q53;
            {var subQ0=sQuery(id+"F0.wireOp",EDGE,"E30.top");var subQ1=sQuery(id+"F0.wireOp",EDGE,"E27");var subQ2=makeQuery(id+"F0.imprint","INTERSECT",VERTEX,{"disambiguationData":[OD(0.0)],"derivedFrom":[subQ1,subQ0]});Q53=makeQuery(id+"F0.imprint","IMPRINT",FACE,{"disambiguationData":[TD([[makeQuery(id+"F0.imprint","IMPRINT",EDGE,{"disambiguationData":[TD([[subQ2,1.0]])],"derivedFrom":subQ1}),-1.0]])]});}
            var Q54;
            {var subQ0=sQuery(id+"F0.wireOp",EDGE,"E29.right");var subQ1=sQuery(id+"F0.wireOp",EDGE,"E27");var subQ2=makeQuery(id+"F0.imprint","INTERSECT",VERTEX,{"disambiguationData":[OD(0.0)],"derivedFrom":[subQ1,subQ0]});Q54=makeQuery(id+"F0.imprint","IMPRINT",FACE,{"disambiguationData":[TD([[makeQuery(id+"F0.imprint","IMPRINT",EDGE,{"disambiguationData":[TD([[subQ2,1.0]])],"derivedFrom":subQ1}),1.0]])]});}
            var Q55;
            {var subQ0=sQuery(id+"F0.wireOp",EDGE,"E30.bottom");var subQ1=sQuery(id+"F0.wireOp",EDGE,"E27");var subQ2=makeQuery(id+"F0.imprint","INTERSECT",VERTEX,{"disambiguationData":[OD(0.0)],"derivedFrom":[subQ1,subQ0]});Q55=makeQuery(id+"F0.imprint","IMPRINT",FACE,{"disambiguationData":[TD([[makeQuery(id+"F0.imprint","IMPRINT",EDGE,{"disambiguationData":[TD([[subQ2,-1.0]])],"derivedFrom":subQ1}),1.0]])]});}
            var Q56;
            {var subQ0=sQuery(id+"F0.wireOp",EDGE,"E29.left");var subQ1=sQuery(id+"F0.wireOp",EDGE,"E27");var subQ2=makeQuery(id+"F0.imprint","INTERSECT",VERTEX,{"disambiguationData":[OD(0.0)],"derivedFrom":[subQ1,subQ0]});Q56=makeQuery(id+"F0.imprint","IMPRINT",FACE,{"disambiguationData":[TD([[makeQuery(id+"F0.imprint","IMPRINT",EDGE,{"disambiguationData":[TD([[subQ2,-1.0]])],"derivedFrom":subQ1}),1.0]])]});}
            var Q57;
            {var subQ0=sQuery(id+"F0.wireOp",EDGE,"E30.top");var subQ1=sQuery(id+"F0.wireOp",EDGE,"E27");var subQ2=makeQuery(id+"F0.imprint","INTERSECT",VERTEX,{"disambiguationData":[OD(0.0)],"derivedFrom":[subQ1,subQ0]});Q57=makeQuery(id+"F0.imprint","IMPRINT",FACE,{"disambiguationData":[TD([[makeQuery(id+"F0.imprint","IMPRINT",EDGE,{"disambiguationData":[TD([[subQ2,-1.0]])],"derivedFrom":subQ1}),1.0]])]});}
            var Q58;
            {var subQ0=sQuery(id+"F0.wireOp",EDGE,"E29.left");var subQ1=sQuery(id+"F0.wireOp",EDGE,"E27");var subQ2=makeQuery(id+"F0.imprint","INTERSECT",VERTEX,{"disambiguationData":[OD(1.0)],"derivedFrom":[subQ1,subQ0]});Q58=makeQuery(id+"F0.imprint","IMPRINT",FACE,{"disambiguationData":[TD([[makeQuery(id+"F0.imprint","IMPRINT",EDGE,{"disambiguationData":[TD([[subQ2,-1.0]])],"derivedFrom":subQ1}),-1.0]])]});}
            var Q59;
            {var subQ0=sQuery(id+"F0.wireOp",EDGE,"E30.top");var subQ1=sQuery(id+"F0.wireOp",EDGE,"E27");var subQ2=makeQuery(id+"F0.imprint","INTERSECT",VERTEX,{"disambiguationData":[OD(1.0)],"derivedFrom":[subQ1,subQ0]});Q59=makeQuery(id+"F0.imprint","IMPRINT",FACE,{"disambiguationData":[TD([[makeQuery(id+"F0.imprint","IMPRINT",EDGE,{"disambiguationData":[TD([[subQ2,-1.0]])],"derivedFrom":subQ1}),-1.0]])]});}
            var Q60;
            {var subQ0=sQuery(id+"F0.wireOp",EDGE,"E30.bottom");var subQ1=sQuery(id+"F0.wireOp",EDGE,"E27");var subQ2=makeQuery(id+"F0.imprint","INTERSECT",VERTEX,{"disambiguationData":[OD(1.0)],"derivedFrom":[subQ1,subQ0]});Q60=makeQuery(id+"F0.imprint","IMPRINT",FACE,{"disambiguationData":[TD([[makeQuery(id+"F0.imprint","IMPRINT",EDGE,{"disambiguationData":[TD([[subQ2,-1.0]])],"derivedFrom":subQ1}),-1.0]])]});}
            var Q61;
            Q61=makeQuery(id+"F0.imprint","IMPRINT",FACE,{"disambiguationData":[TD([[makeQuery(id+"F0.imprint","IMPRINT",EDGE,{"derivedFrom":sQuery(id+"F0.wireOp",EDGE,"E28")}),1.0]])]});
            var Q62;
            {var subQ0=sQuery(id+"F0.wireOp",EDGE,"E29.right");var subQ1=sQuery(id+"F0.wireOp",EDGE,"E20");var subQ2=makeQuery(id+"F0.imprint","INTERSECT",VERTEX,{"disambiguationData":[OD(0.0)],"derivedFrom":[subQ1,subQ0]});Q62=makeQuery(id+"F0.imprint","IMPRINT",FACE,{"disambiguationData":[TD([[makeQuery(id+"F0.imprint","IMPRINT",EDGE,{"disambiguationData":[TD([[subQ2,-1.0]])],"derivedFrom":subQ1}),1.0]])]});}
            var Q63;
            {var subQ0=sQuery(id+"F0.wireOp",EDGE,"E29.left");var subQ1=sQuery(id+"F0.wireOp",EDGE,"E22");var subQ2=makeQuery(id+"F0.imprint","INTERSECT",VERTEX,{"disambiguationData":[OD(1.0)],"derivedFrom":[subQ1,subQ0]});Q63=makeQuery(id+"F0.imprint","IMPRINT",FACE,{"disambiguationData":[TD([[makeQuery(id+"F0.imprint","IMPRINT",EDGE,{"disambiguationData":[TD([[subQ2,-1.0]])],"derivedFrom":subQ1}),1.0]])]});}
            var Q64;
            {var subQ0=sQuery(id+"F0.wireOp",EDGE,"E29.right");var subQ1=sQuery(id+"F0.wireOp",EDGE,"E14");var subQ2=makeQuery(id+"F0.imprint","INTERSECT",VERTEX,{"disambiguationData":[OD(0.0)],"derivedFrom":[subQ1,subQ0]});Q64=makeQuery(id+"F0.imprint","IMPRINT",FACE,{"disambiguationData":[TD([[makeQuery(id+"F0.imprint","IMPRINT",EDGE,{"disambiguationData":[TD([[subQ2,-1.0]])],"derivedFrom":subQ1}),1.0]])]});}
            var Q65;
            {var subQ0=sQuery(id+"F0.wireOp",EDGE,"E29.right");var subQ1=sQuery(id+"F0.wireOp",EDGE,"E24");var subQ2=makeQuery(id+"F0.imprint","INTERSECT",VERTEX,{"disambiguationData":[OD(0.0)],"derivedFrom":[subQ1,subQ0]});Q65=makeQuery(id+"F0.imprint","IMPRINT",FACE,{"disambiguationData":[TD([[makeQuery(id+"F0.imprint","IMPRINT",EDGE,{"disambiguationData":[TD([[subQ2,-1.0]])],"derivedFrom":subQ1}),1.0]])]});}
            var Q66;
            {var subQ0=sQuery(id+"F0.wireOp",EDGE,"E29.left");var subQ1=sQuery(id+"F0.wireOp",EDGE,"E6");var subQ2=makeQuery(id+"F0.imprint","INTERSECT",VERTEX,{"disambiguationData":[OD(1.0)],"derivedFrom":[subQ1,subQ0]});Q66=makeQuery(id+"F0.imprint","IMPRINT",FACE,{"disambiguationData":[TD([[makeQuery(id+"F0.imprint","IMPRINT",EDGE,{"disambiguationData":[TD([[subQ2,-1.0]])],"derivedFrom":subQ1}),1.0]])]});}
            var Q67;
            {var subQ0=sQuery(id+"F0.wireOp",EDGE,"E29.right");var subQ1=sQuery(id+"F0.wireOp",EDGE,"E18");var subQ2=makeQuery(id+"F0.imprint","INTERSECT",VERTEX,{"disambiguationData":[OD(0.0)],"derivedFrom":[subQ1,subQ0]});Q67=makeQuery(id+"F0.imprint","IMPRINT",FACE,{"disambiguationData":[TD([[makeQuery(id+"F0.imprint","IMPRINT",EDGE,{"disambiguationData":[TD([[subQ2,-1.0]])],"derivedFrom":subQ1}),1.0]])]});}
            var Q68;
            {var subQ0=sQuery(id+"F0.wireOp",EDGE,"E29.left");var subQ1=sQuery(id+"F0.wireOp",EDGE,"E4");var subQ2=makeQuery(id+"F0.imprint","INTERSECT",VERTEX,{"disambiguationData":[OD(1.0)],"derivedFrom":[subQ1,subQ0]});Q68=makeQuery(id+"F0.imprint","IMPRINT",FACE,{"disambiguationData":[TD([[makeQuery(id+"F0.imprint","IMPRINT",EDGE,{"disambiguationData":[TD([[subQ2,-1.0]])],"derivedFrom":subQ1}),1.0]])]});}
            var Q69;
            {var subQ0=sQuery(id+"F0.wireOp",EDGE,"E29.left");var subQ1=sQuery(id+"F0.wireOp",EDGE,"E18");var subQ2=makeQuery(id+"F0.imprint","INTERSECT",VERTEX,{"disambiguationData":[OD(1.0)],"derivedFrom":[subQ1,subQ0]});Q69=makeQuery(id+"F0.imprint","IMPRINT",FACE,{"disambiguationData":[TD([[makeQuery(id+"F0.imprint","IMPRINT",EDGE,{"disambiguationData":[TD([[subQ2,-1.0]])],"derivedFrom":subQ1}),1.0]])]});}
            var Q70;
            {var subQ0=sQuery(id+"F0.wireOp",EDGE,"E29.left");var subQ1=sQuery(id+"F0.wireOp",EDGE,"E16");var subQ2=makeQuery(id+"F0.imprint","INTERSECT",VERTEX,{"disambiguationData":[OD(1.0)],"derivedFrom":[subQ1,subQ0]});Q70=makeQuery(id+"F0.imprint","IMPRINT",FACE,{"disambiguationData":[TD([[makeQuery(id+"F0.imprint","IMPRINT",EDGE,{"disambiguationData":[TD([[subQ2,-1.0]])],"derivedFrom":subQ1}),1.0]])]});}
            var Q71;
            {var subQ1=sQuery(id+"F0.wireOp",EDGE,"E26");var subQ5=sQuery(id+"F0.wireOp",EDGE,"E29.left");var subQ6=makeQuery(id+"F0.imprint","INTERSECT",VERTEX,{"disambiguationData":[OD(1.0)],"derivedFrom":[subQ1,subQ5]});Q71=makeQuery(id+"F0.imprint","IMPRINT",FACE,{"disambiguationData":[TD([[makeQuery(id+"F0.imprint","IMPRINT",EDGE,{"disambiguationData":[TD([[subQ6,-1.0]])],"derivedFrom":subQ1}),1.0]])]});}
            var Q72;
            {var subQ0=sQuery(id+"F0.wireOp",EDGE,"E29.left");var subQ1=sQuery(id+"F0.wireOp",EDGE,"E14");var subQ2=makeQuery(id+"F0.imprint","INTERSECT",VERTEX,{"disambiguationData":[OD(1.0)],"derivedFrom":[subQ1,subQ0]});Q72=makeQuery(id+"F0.imprint","IMPRINT",FACE,{"disambiguationData":[TD([[makeQuery(id+"F0.imprint","IMPRINT",EDGE,{"disambiguationData":[TD([[subQ2,-1.0]])],"derivedFrom":subQ1}),1.0]])]});}
            var Q73;
            {var subQ0=sQuery(id+"F0.wireOp",EDGE,"E29.left");var subQ1=sQuery(id+"F0.wireOp",EDGE,"E24");var subQ2=makeQuery(id+"F0.imprint","INTERSECT",VERTEX,{"disambiguationData":[OD(1.0)],"derivedFrom":[subQ1,subQ0]});Q73=makeQuery(id+"F0.imprint","IMPRINT",FACE,{"disambiguationData":[TD([[makeQuery(id+"F0.imprint","IMPRINT",EDGE,{"disambiguationData":[TD([[subQ2,-1.0]])],"derivedFrom":subQ1}),1.0]])]});}
            var Q74;
            {var subQ0=sQuery(id+"F0.wireOp",EDGE,"E29.left");var subQ1=sQuery(id+"F0.wireOp",EDGE,"E20");var subQ2=makeQuery(id+"F0.imprint","INTERSECT",VERTEX,{"disambiguationData":[OD(1.0)],"derivedFrom":[subQ1,subQ0]});Q74=makeQuery(id+"F0.imprint","IMPRINT",FACE,{"disambiguationData":[TD([[makeQuery(id+"F0.imprint","IMPRINT",EDGE,{"disambiguationData":[TD([[subQ2,-1.0]])],"derivedFrom":subQ1}),1.0]])]});}
            var Q75;
            {var subQ0=sQuery(id+"F0.wireOp",EDGE,"E29.right");var subQ1=sQuery(id+"F0.wireOp",EDGE,"E16");var subQ2=makeQuery(id+"F0.imprint","INTERSECT",VERTEX,{"disambiguationData":[OD(0.0)],"derivedFrom":[subQ1,subQ0]});Q75=makeQuery(id+"F0.imprint","IMPRINT",FACE,{"disambiguationData":[TD([[makeQuery(id+"F0.imprint","IMPRINT",EDGE,{"disambiguationData":[TD([[subQ2,-1.0]])],"derivedFrom":subQ1}),1.0]])]});}
            var Q76;
            {var subQ0=sQuery(id+"F0.wireOp",EDGE,"E29.right");var subQ1=sQuery(id+"F0.wireOp",EDGE,"E2");var subQ2=makeQuery(id+"F0.imprint","INTERSECT",VERTEX,{"disambiguationData":[OD(0.0)],"derivedFrom":[subQ1,subQ0]});Q76=makeQuery(id+"F0.imprint","IMPRINT",FACE,{"disambiguationData":[TD([[makeQuery(id+"F0.imprint","IMPRINT",EDGE,{"disambiguationData":[TD([[subQ2,-1.0]])],"derivedFrom":subQ1}),1.0]])]});}
            var Q77;
            {var subQ0=sQuery(id+"F0.wireOp",EDGE,"E29.left");var subQ1=sQuery(id+"F0.wireOp",EDGE,"E8");var subQ2=makeQuery(id+"F0.imprint","INTERSECT",VERTEX,{"disambiguationData":[OD(1.0)],"derivedFrom":[subQ1,subQ0]});Q77=makeQuery(id+"F0.imprint","IMPRINT",FACE,{"disambiguationData":[TD([[makeQuery(id+"F0.imprint","IMPRINT",EDGE,{"disambiguationData":[TD([[subQ2,-1.0]])],"derivedFrom":subQ1}),1.0]])]});}
            var Q78;
            {var subQ0=sQuery(id+"F0.wireOp",EDGE,"E29.left");var subQ1=sQuery(id+"F0.wireOp",EDGE,"E12");var subQ2=makeQuery(id+"F0.imprint","INTERSECT",VERTEX,{"disambiguationData":[OD(1.0)],"derivedFrom":[subQ1,subQ0]});Q78=makeQuery(id+"F0.imprint","IMPRINT",FACE,{"disambiguationData":[TD([[makeQuery(id+"F0.imprint","IMPRINT",EDGE,{"disambiguationData":[TD([[subQ2,-1.0]])],"derivedFrom":subQ1}),1.0]])]});}
            var Q79;
            {var subQ0=sQuery(id+"F0.wireOp",EDGE,"E29.left");var subQ1=sQuery(id+"F0.wireOp",EDGE,"E2");var subQ2=makeQuery(id+"F0.imprint","INTERSECT",VERTEX,{"disambiguationData":[OD(1.0)],"derivedFrom":[subQ1,subQ0]});Q79=makeQuery(id+"F0.imprint","IMPRINT",FACE,{"disambiguationData":[TD([[makeQuery(id+"F0.imprint","IMPRINT",EDGE,{"disambiguationData":[TD([[subQ2,-1.0]])],"derivedFrom":subQ1}),1.0]])]});}
            var Q80;
            {var subQ0=sQuery(id+"F0.wireOp",EDGE,"E29.right");var subQ1=sQuery(id+"F0.wireOp",EDGE,"E22");var subQ2=makeQuery(id+"F0.imprint","INTERSECT",VERTEX,{"disambiguationData":[OD(0.0)],"derivedFrom":[subQ1,subQ0]});Q80=makeQuery(id+"F0.imprint","IMPRINT",FACE,{"disambiguationData":[TD([[makeQuery(id+"F0.imprint","IMPRINT",EDGE,{"disambiguationData":[TD([[subQ2,-1.0]])],"derivedFrom":subQ1}),1.0]])]});}
            var Q81;
            {var subQ0=sQuery(id+"F0.wireOp",EDGE,"E29.right");var subQ1=sQuery(id+"F0.wireOp",EDGE,"E8");var subQ2=makeQuery(id+"F0.imprint","INTERSECT",VERTEX,{"disambiguationData":[OD(0.0)],"derivedFrom":[subQ1,subQ0]});Q81=makeQuery(id+"F0.imprint","IMPRINT",FACE,{"disambiguationData":[TD([[makeQuery(id+"F0.imprint","IMPRINT",EDGE,{"disambiguationData":[TD([[subQ2,-1.0]])],"derivedFrom":subQ1}),1.0]])]});}
            var Q82;
            {var subQ0=sQuery(id+"F0.wireOp",EDGE,"E29.left");var subQ1=sQuery(id+"F0.wireOp",EDGE,"E10");var subQ2=makeQuery(id+"F0.imprint","INTERSECT",VERTEX,{"disambiguationData":[OD(1.0)],"derivedFrom":[subQ1,subQ0]});Q82=makeQuery(id+"F0.imprint","IMPRINT",FACE,{"disambiguationData":[TD([[makeQuery(id+"F0.imprint","IMPRINT",EDGE,{"disambiguationData":[TD([[subQ2,-1.0]])],"derivedFrom":subQ1}),1.0]])]});}
            var Q83;
            {var subQ0=sQuery(id+"F0.wireOp",EDGE,"E29.right");var subQ1=sQuery(id+"F0.wireOp",EDGE,"E10");var subQ2=makeQuery(id+"F0.imprint","INTERSECT",VERTEX,{"disambiguationData":[OD(0.0)],"derivedFrom":[subQ1,subQ0]});Q83=makeQuery(id+"F0.imprint","IMPRINT",FACE,{"disambiguationData":[TD([[makeQuery(id+"F0.imprint","IMPRINT",EDGE,{"disambiguationData":[TD([[subQ2,-1.0]])],"derivedFrom":subQ1}),1.0]])]});}
            var Q84;
            {var subQ0=sQuery(id+"F0.wireOp",EDGE,"E29.right");var subQ1=sQuery(id+"F0.wireOp",EDGE,"E12");var subQ2=makeQuery(id+"F0.imprint","INTERSECT",VERTEX,{"disambiguationData":[OD(0.0)],"derivedFrom":[subQ1,subQ0]});Q84=makeQuery(id+"F0.imprint","IMPRINT",FACE,{"disambiguationData":[TD([[makeQuery(id+"F0.imprint","IMPRINT",EDGE,{"disambiguationData":[TD([[subQ2,-1.0]])],"derivedFrom":subQ1}),1.0]])]});}
            var Q85;
            {var subQ0=sQuery(id+"F0.wireOp",EDGE,"E29.right");var subQ1=sQuery(id+"F0.wireOp",EDGE,"E6");var subQ2=makeQuery(id+"F0.imprint","INTERSECT",VERTEX,{"disambiguationData":[OD(0.0)],"derivedFrom":[subQ1,subQ0]});Q85=makeQuery(id+"F0.imprint","IMPRINT",FACE,{"disambiguationData":[TD([[makeQuery(id+"F0.imprint","IMPRINT",EDGE,{"disambiguationData":[TD([[subQ2,-1.0]])],"derivedFrom":subQ1}),1.0]])]});}
            var Q86;
            {var subQ0=sQuery(id+"F0.wireOp",EDGE,"E29.right");var subQ1=sQuery(id+"F0.wireOp",EDGE,"E7");var subQ2=makeQuery(id+"F0.imprint","INTERSECT",VERTEX,{"disambiguationData":[OD(0.0)],"derivedFrom":[subQ1,subQ0]});Q86=makeQuery(id+"F0.imprint","IMPRINT",FACE,{"disambiguationData":[TD([[makeQuery(id+"F0.imprint","IMPRINT",EDGE,{"disambiguationData":[TD([[subQ2,-1.0]])],"derivedFrom":subQ1}),1.0]])]});}
            var Q87;
            {var subQ0=sQuery(id+"F0.wireOp",EDGE,"E29.right");var subQ1=sQuery(id+"F0.wireOp",EDGE,"E5");var subQ2=makeQuery(id+"F0.imprint","INTERSECT",VERTEX,{"disambiguationData":[OD(0.0)],"derivedFrom":[subQ1,subQ0]});Q87=makeQuery(id+"F0.imprint","IMPRINT",FACE,{"disambiguationData":[TD([[makeQuery(id+"F0.imprint","IMPRINT",EDGE,{"disambiguationData":[TD([[subQ2,-1.0]])],"derivedFrom":subQ1}),1.0]])]});}
            var Q88;
            {var subQ0=sQuery(id+"F0.wireOp",EDGE,"E29.right");var subQ1=sQuery(id+"F0.wireOp",EDGE,"E4");var subQ2=makeQuery(id+"F0.imprint","INTERSECT",VERTEX,{"disambiguationData":[OD(0.0)],"derivedFrom":[subQ1,subQ0]});Q88=makeQuery(id+"F0.imprint","IMPRINT",FACE,{"disambiguationData":[TD([[makeQuery(id+"F0.imprint","IMPRINT",EDGE,{"disambiguationData":[TD([[subQ2,-1.0]])],"derivedFrom":subQ1}),1.0]])]});}
            var Q89;
            {var subQ0=sQuery(id+"F0.wireOp",EDGE,"E29.right");var subQ1=sQuery(id+"F0.wireOp",EDGE,"E9");var subQ2=makeQuery(id+"F0.imprint","INTERSECT",VERTEX,{"disambiguationData":[OD(0.0)],"derivedFrom":[subQ1,subQ0]});Q89=makeQuery(id+"F0.imprint","IMPRINT",FACE,{"disambiguationData":[TD([[makeQuery(id+"F0.imprint","IMPRINT",EDGE,{"disambiguationData":[TD([[subQ2,-1.0]])],"derivedFrom":subQ1}),1.0]])]});}
            var Q90;
            {var subQ0=sQuery(id+"F0.wireOp",EDGE,"E29.left");var subQ1=sQuery(id+"F0.wireOp",EDGE,"E1");var subQ2=makeQuery(id+"F0.imprint","INTERSECT",VERTEX,{"disambiguationData":[OD(1.0)],"derivedFrom":[subQ1,subQ0]});Q90=makeQuery(id+"F0.imprint","IMPRINT",FACE,{"disambiguationData":[TD([[makeQuery(id+"F0.imprint","IMPRINT",EDGE,{"disambiguationData":[TD([[subQ2,-1.0]])],"derivedFrom":subQ1}),1.0]])]});}
            var Q91;
            {var subQ0=sQuery(id+"F0.wireOp",EDGE,"E29.right");var subQ1=sQuery(id+"F0.wireOp",EDGE,"E3");var subQ2=makeQuery(id+"F0.imprint","INTERSECT",VERTEX,{"disambiguationData":[OD(0.0)],"derivedFrom":[subQ1,subQ0]});Q91=makeQuery(id+"F0.imprint","IMPRINT",FACE,{"disambiguationData":[TD([[makeQuery(id+"F0.imprint","IMPRINT",EDGE,{"disambiguationData":[TD([[subQ2,-1.0]])],"derivedFrom":subQ1}),1.0]])]});}
            var Q92;
            {var subQ0=sQuery(id+"F0.wireOp",EDGE,"E29.right");var subQ1=sQuery(id+"F0.wireOp",EDGE,"E17");var subQ2=makeQuery(id+"F0.imprint","INTERSECT",VERTEX,{"disambiguationData":[OD(0.0)],"derivedFrom":[subQ1,subQ0]});Q92=makeQuery(id+"F0.imprint","IMPRINT",FACE,{"disambiguationData":[TD([[makeQuery(id+"F0.imprint","IMPRINT",EDGE,{"disambiguationData":[TD([[subQ2,-1.0]])],"derivedFrom":subQ1}),1.0]])]});}
            var Q93;
            {var subQ0=sQuery(id+"F0.wireOp",EDGE,"E29.right");var subQ1=sQuery(id+"F0.wireOp",EDGE,"E15");var subQ2=makeQuery(id+"F0.imprint","INTERSECT",VERTEX,{"disambiguationData":[OD(0.0)],"derivedFrom":[subQ1,subQ0]});Q93=makeQuery(id+"F0.imprint","IMPRINT",FACE,{"disambiguationData":[TD([[makeQuery(id+"F0.imprint","IMPRINT",EDGE,{"disambiguationData":[TD([[subQ2,-1.0]])],"derivedFrom":subQ1}),1.0]])]});}
            var Q94;
            {var subQ0=sQuery(id+"F0.wireOp",EDGE,"E29.right");var subQ1=sQuery(id+"F0.wireOp",EDGE,"E13");var subQ2=makeQuery(id+"F0.imprint","INTERSECT",VERTEX,{"disambiguationData":[OD(0.0)],"derivedFrom":[subQ1,subQ0]});Q94=makeQuery(id+"F0.imprint","IMPRINT",FACE,{"disambiguationData":[TD([[makeQuery(id+"F0.imprint","IMPRINT",EDGE,{"disambiguationData":[TD([[subQ2,-1.0]])],"derivedFrom":subQ1}),1.0]])]});}
            var Q95;
            {var subQ0=sQuery(id+"F0.wireOp",EDGE,"E29.right");var subQ1=sQuery(id+"F0.wireOp",EDGE,"E11");var subQ2=makeQuery(id+"F0.imprint","INTERSECT",VERTEX,{"disambiguationData":[OD(0.0)],"derivedFrom":[subQ1,subQ0]});Q95=makeQuery(id+"F0.imprint","IMPRINT",FACE,{"disambiguationData":[TD([[makeQuery(id+"F0.imprint","IMPRINT",EDGE,{"disambiguationData":[TD([[subQ2,-1.0]])],"derivedFrom":subQ1}),1.0]])]});}
            var Q96;
            {var subQ0=sQuery(id+"F0.wireOp",EDGE,"E29.right");var subQ1=sQuery(id+"F0.wireOp",EDGE,"E25");var subQ2=makeQuery(id+"F0.imprint","INTERSECT",VERTEX,{"disambiguationData":[OD(0.0)],"derivedFrom":[subQ1,subQ0]});Q96=makeQuery(id+"F0.imprint","IMPRINT",FACE,{"disambiguationData":[TD([[makeQuery(id+"F0.imprint","IMPRINT",EDGE,{"disambiguationData":[TD([[subQ2,-1.0]])],"derivedFrom":subQ1}),1.0]])]});}
            var Q97;
            {var subQ0=sQuery(id+"F0.wireOp",EDGE,"E29.right");var subQ1=sQuery(id+"F0.wireOp",EDGE,"E23");var subQ2=makeQuery(id+"F0.imprint","INTERSECT",VERTEX,{"disambiguationData":[OD(0.0)],"derivedFrom":[subQ1,subQ0]});Q97=makeQuery(id+"F0.imprint","IMPRINT",FACE,{"disambiguationData":[TD([[makeQuery(id+"F0.imprint","IMPRINT",EDGE,{"disambiguationData":[TD([[subQ2,-1.0]])],"derivedFrom":subQ1}),1.0]])]});}
            var Q98;
            {var subQ0=sQuery(id+"F0.wireOp",EDGE,"E29.right");var subQ1=sQuery(id+"F0.wireOp",EDGE,"E21");var subQ2=makeQuery(id+"F0.imprint","INTERSECT",VERTEX,{"disambiguationData":[OD(0.0)],"derivedFrom":[subQ1,subQ0]});Q98=makeQuery(id+"F0.imprint","IMPRINT",FACE,{"disambiguationData":[TD([[makeQuery(id+"F0.imprint","IMPRINT",EDGE,{"disambiguationData":[TD([[subQ2,-1.0]])],"derivedFrom":subQ1}),1.0]])]});}
            var Q99;
            {var subQ0=sQuery(id+"F0.wireOp",EDGE,"E29.right");var subQ1=sQuery(id+"F0.wireOp",EDGE,"E19");var subQ2=makeQuery(id+"F0.imprint","INTERSECT",VERTEX,{"disambiguationData":[OD(0.0)],"derivedFrom":[subQ1,subQ0]});Q99=makeQuery(id+"F0.imprint","IMPRINT",FACE,{"disambiguationData":[TD([[makeQuery(id+"F0.imprint","IMPRINT",EDGE,{"disambiguationData":[TD([[subQ2,-1.0]])],"derivedFrom":subQ1}),1.0]])]});}
            var Q100;
            {var subQ0=sQuery(id+"F0.wireOp",EDGE,"E29.right");var subQ1=sQuery(id+"F0.wireOp",EDGE,"E1");var subQ2=makeQuery(id+"F0.imprint","INTERSECT",VERTEX,{"disambiguationData":[OD(0.0)],"derivedFrom":[subQ1,subQ0]});Q100=makeQuery(id+"F0.imprint","IMPRINT",FACE,{"disambiguationData":[TD([[makeQuery(id+"F0.imprint","IMPRINT",EDGE,{"disambiguationData":[TD([[subQ2,-1.0]])],"derivedFrom":subQ1}),1.0]])]});}
            var Q101;
            {var subQ0=sQuery(id+"F0.wireOp",EDGE,"E29.left");var subQ1=sQuery(id+"F0.wireOp",EDGE,"E13");var subQ2=makeQuery(id+"F0.imprint","INTERSECT",VERTEX,{"disambiguationData":[OD(1.0)],"derivedFrom":[subQ1,subQ0]});Q101=makeQuery(id+"F0.imprint","IMPRINT",FACE,{"disambiguationData":[TD([[makeQuery(id+"F0.imprint","IMPRINT",EDGE,{"disambiguationData":[TD([[subQ2,-1.0]])],"derivedFrom":subQ1}),1.0]])]});}
            var Q102;
            {var subQ0=sQuery(id+"F0.wireOp",EDGE,"E29.left");var subQ1=sQuery(id+"F0.wireOp",EDGE,"E11");var subQ2=makeQuery(id+"F0.imprint","INTERSECT",VERTEX,{"disambiguationData":[OD(1.0)],"derivedFrom":[subQ1,subQ0]});Q102=makeQuery(id+"F0.imprint","IMPRINT",FACE,{"disambiguationData":[TD([[makeQuery(id+"F0.imprint","IMPRINT",EDGE,{"disambiguationData":[TD([[subQ2,-1.0]])],"derivedFrom":subQ1}),1.0]])]});}
            var Q103;
            {var subQ0=sQuery(id+"F0.wireOp",EDGE,"E29.left");var subQ1=sQuery(id+"F0.wireOp",EDGE,"E9");var subQ2=makeQuery(id+"F0.imprint","INTERSECT",VERTEX,{"disambiguationData":[OD(1.0)],"derivedFrom":[subQ1,subQ0]});Q103=makeQuery(id+"F0.imprint","IMPRINT",FACE,{"disambiguationData":[TD([[makeQuery(id+"F0.imprint","IMPRINT",EDGE,{"disambiguationData":[TD([[subQ2,-1.0]])],"derivedFrom":subQ1}),1.0]])]});}
            var Q104;
            {var subQ0=sQuery(id+"F0.wireOp",EDGE,"E29.left");var subQ1=sQuery(id+"F0.wireOp",EDGE,"E7");var subQ2=makeQuery(id+"F0.imprint","INTERSECT",VERTEX,{"disambiguationData":[OD(1.0)],"derivedFrom":[subQ1,subQ0]});Q104=makeQuery(id+"F0.imprint","IMPRINT",FACE,{"disambiguationData":[TD([[makeQuery(id+"F0.imprint","IMPRINT",EDGE,{"disambiguationData":[TD([[subQ2,-1.0]])],"derivedFrom":subQ1}),1.0]])]});}
            var Q105;
            {var subQ0=sQuery(id+"F0.wireOp",EDGE,"E29.left");var subQ1=sQuery(id+"F0.wireOp",EDGE,"E21");var subQ2=makeQuery(id+"F0.imprint","INTERSECT",VERTEX,{"disambiguationData":[OD(1.0)],"derivedFrom":[subQ1,subQ0]});Q105=makeQuery(id+"F0.imprint","IMPRINT",FACE,{"disambiguationData":[TD([[makeQuery(id+"F0.imprint","IMPRINT",EDGE,{"disambiguationData":[TD([[subQ2,-1.0]])],"derivedFrom":subQ1}),1.0]])]});}
            var Q106;
            {var subQ0=sQuery(id+"F0.wireOp",EDGE,"E29.left");var subQ1=sQuery(id+"F0.wireOp",EDGE,"E19");var subQ2=makeQuery(id+"F0.imprint","INTERSECT",VERTEX,{"disambiguationData":[OD(1.0)],"derivedFrom":[subQ1,subQ0]});Q106=makeQuery(id+"F0.imprint","IMPRINT",FACE,{"disambiguationData":[TD([[makeQuery(id+"F0.imprint","IMPRINT",EDGE,{"disambiguationData":[TD([[subQ2,-1.0]])],"derivedFrom":subQ1}),1.0]])]});}
            var Q107;
            {var subQ0=sQuery(id+"F0.wireOp",EDGE,"E29.left");var subQ1=sQuery(id+"F0.wireOp",EDGE,"E17");var subQ2=makeQuery(id+"F0.imprint","INTERSECT",VERTEX,{"disambiguationData":[OD(1.0)],"derivedFrom":[subQ1,subQ0]});Q107=makeQuery(id+"F0.imprint","IMPRINT",FACE,{"disambiguationData":[TD([[makeQuery(id+"F0.imprint","IMPRINT",EDGE,{"disambiguationData":[TD([[subQ2,-1.0]])],"derivedFrom":subQ1}),1.0]])]});}
            var Q108;
            {var subQ0=sQuery(id+"F0.wireOp",EDGE,"E29.left");var subQ1=sQuery(id+"F0.wireOp",EDGE,"E15");var subQ2=makeQuery(id+"F0.imprint","INTERSECT",VERTEX,{"disambiguationData":[OD(1.0)],"derivedFrom":[subQ1,subQ0]});Q108=makeQuery(id+"F0.imprint","IMPRINT",FACE,{"disambiguationData":[TD([[makeQuery(id+"F0.imprint","IMPRINT",EDGE,{"disambiguationData":[TD([[subQ2,-1.0]])],"derivedFrom":subQ1}),1.0]])]});}
            var Q109;
            {var subQ0=sQuery(id+"F0.wireOp",EDGE,"E29.left");var subQ1=sQuery(id+"F0.wireOp",EDGE,"E25");var subQ2=makeQuery(id+"F0.imprint","INTERSECT",VERTEX,{"disambiguationData":[OD(1.0)],"derivedFrom":[subQ1,subQ0]});Q109=makeQuery(id+"F0.imprint","IMPRINT",FACE,{"disambiguationData":[TD([[makeQuery(id+"F0.imprint","IMPRINT",EDGE,{"disambiguationData":[TD([[subQ2,-1.0]])],"derivedFrom":subQ1}),1.0]])]});}
            var Q110;
            {var subQ0=sQuery(id+"F0.wireOp",EDGE,"E29.left");var subQ1=sQuery(id+"F0.wireOp",EDGE,"E23");var subQ2=makeQuery(id+"F0.imprint","INTERSECT",VERTEX,{"disambiguationData":[OD(1.0)],"derivedFrom":[subQ1,subQ0]});Q110=makeQuery(id+"F0.imprint","IMPRINT",FACE,{"disambiguationData":[TD([[makeQuery(id+"F0.imprint","IMPRINT",EDGE,{"disambiguationData":[TD([[subQ2,-1.0]])],"derivedFrom":subQ1}),1.0]])]});}
            var Q111;
            {var subQ0=sQuery(id+"F0.wireOp",EDGE,"E29.left");var subQ1=sQuery(id+"F0.wireOp",EDGE,"E5");var subQ2=makeQuery(id+"F0.imprint","INTERSECT",VERTEX,{"disambiguationData":[OD(1.0)],"derivedFrom":[subQ1,subQ0]});Q111=makeQuery(id+"F0.imprint","IMPRINT",FACE,{"disambiguationData":[TD([[makeQuery(id+"F0.imprint","IMPRINT",EDGE,{"disambiguationData":[TD([[subQ2,-1.0]])],"derivedFrom":subQ1}),1.0]])]});}
            var Q112;
            {var subQ0=sQuery(id+"F0.wireOp",EDGE,"E29.left");var subQ1=sQuery(id+"F0.wireOp",EDGE,"E3");var subQ2=makeQuery(id+"F0.imprint","INTERSECT",VERTEX,{"disambiguationData":[OD(1.0)],"derivedFrom":[subQ1,subQ0]});Q112=makeQuery(id+"F0.imprint","IMPRINT",FACE,{"disambiguationData":[TD([[makeQuery(id+"F0.imprint","IMPRINT",EDGE,{"disambiguationData":[TD([[subQ2,-1.0]])],"derivedFrom":subQ1}),1.0]])]});}
            var Q113;
            {var subQ0=sQuery(id+"F0.wireOp",EDGE,"E29.right");var subQ1=sQuery(id+"F0.wireOp",EDGE,"E26");var subQ2=makeQuery(id+"F0.imprint","INTERSECT",VERTEX,{"disambiguationData":[OD(0.0)],"derivedFrom":[subQ1,subQ0]});Q113=makeQuery(id+"F0.imprint","IMPRINT",FACE,{"disambiguationData":[TD([[makeQuery(id+"F0.imprint","IMPRINT",EDGE,{"disambiguationData":[TD([[subQ2,-1.0]])],"derivedFrom":subQ1}),1.0]])]});}
            var Q114;
            {var subQ0=sQuery(id+"F0.wireOp",EDGE,"E29.left");var subQ1=sQuery(id+"F0.wireOp",EDGE,"E26");var subQ2=makeQuery(id+"F0.imprint","INTERSECT",VERTEX,{"disambiguationData":[OD(0.0)],"derivedFrom":[subQ1,subQ0]});Q114=makeQuery(id+"F0.imprint","IMPRINT",FACE,{"disambiguationData":[TD([[makeQuery(id+"F0.imprint","IMPRINT",EDGE,{"disambiguationData":[TD([[subQ2,-1.0]])],"derivedFrom":subQ1}),1.0]])]});}
            var Q115;
            {var subQ0=sQuery(id+"F0.wireOp",EDGE,"E30.bottom");var subQ1=sQuery(id+"F0.wireOp",EDGE,"E25");var subQ2=makeQuery(id+"F0.imprint","INTERSECT",VERTEX,{"disambiguationData":[OD(0.0)],"derivedFrom":[subQ1,subQ0]});Q115=makeQuery(id+"F0.imprint","IMPRINT",FACE,{"disambiguationData":[TD([[makeQuery(id+"F0.imprint","IMPRINT",EDGE,{"disambiguationData":[TD([[subQ2,-1.0]])],"derivedFrom":subQ1}),1.0]])]});}
            var Q116;
            {var subQ0=sQuery(id+"F0.wireOp",EDGE,"E30.bottom");var subQ1=sQuery(id+"F0.wireOp",EDGE,"E26");var subQ2=makeQuery(id+"F0.imprint","INTERSECT",VERTEX,{"disambiguationData":[OD(0.0)],"derivedFrom":[subQ1,subQ0]});Q116=makeQuery(id+"F0.imprint","IMPRINT",FACE,{"disambiguationData":[TD([[makeQuery(id+"F0.imprint","IMPRINT",EDGE,{"disambiguationData":[TD([[subQ2,-1.0]])],"derivedFrom":subQ1}),1.0]])]});}
            var Q117;
            {var subQ0=sQuery(id+"F0.wireOp",EDGE,"E29.left");var subQ1=sQuery(id+"F0.wireOp",EDGE,"E25");var subQ2=makeQuery(id+"F0.imprint","INTERSECT",VERTEX,{"disambiguationData":[OD(0.0)],"derivedFrom":[subQ1,subQ0]});Q117=makeQuery(id+"F0.imprint","IMPRINT",FACE,{"disambiguationData":[TD([[makeQuery(id+"F0.imprint","IMPRINT",EDGE,{"disambiguationData":[TD([[subQ2,-1.0]])],"derivedFrom":subQ1}),1.0]])]});}
            var Q118;
            {var subQ0=sQuery(id+"F0.wireOp",EDGE,"E29.right");var subQ1=sQuery(id+"F0.wireOp",EDGE,"E25");var subQ2=makeQuery(id+"F0.imprint","INTERSECT",VERTEX,{"disambiguationData":[OD(0.0)],"derivedFrom":[subQ1,subQ0]});Q118=makeQuery(id+"F0.imprint","IMPRINT",FACE,{"disambiguationData":[TD([[makeQuery(id+"F0.imprint","IMPRINT",EDGE,{"disambiguationData":[TD([[subQ2,1.0]])],"derivedFrom":subQ1}),1.0]])]});}
            var Q119;
            {var subQ0=sQuery(id+"F0.wireOp",EDGE,"E29.right");var subQ1=sQuery(id+"F0.wireOp",EDGE,"E26");var subQ2=makeQuery(id+"F0.imprint","INTERSECT",VERTEX,{"disambiguationData":[OD(0.0)],"derivedFrom":[subQ1,subQ0]});Q119=makeQuery(id+"F0.imprint","IMPRINT",FACE,{"disambiguationData":[TD([[makeQuery(id+"F0.imprint","IMPRINT",EDGE,{"disambiguationData":[TD([[subQ2,1.0]])],"derivedFrom":subQ1}),1.0]])]});}
            var Q120;
            {var subQ0=sQuery(id+"F0.wireOp",EDGE,"E29.right");var subQ1=sQuery(id+"F0.wireOp",EDGE,"E26");var subQ2=makeQuery(id+"F0.imprint","INTERSECT",VERTEX,{"disambiguationData":[OD(1.0)],"derivedFrom":[subQ1,subQ0]});Q120=makeQuery(id+"F0.imprint","IMPRINT",FACE,{"disambiguationData":[TD([[makeQuery(id+"F0.imprint","IMPRINT",EDGE,{"disambiguationData":[TD([[subQ2,-1.0]])],"derivedFrom":subQ1}),1.0]])]});}
            var Q121;
            {var subQ0=sQuery(id+"F0.wireOp",EDGE,"E29.right");var subQ1=sQuery(id+"F0.wireOp",EDGE,"E25");var subQ2=makeQuery(id+"F0.imprint","INTERSECT",VERTEX,{"disambiguationData":[OD(1.0)],"derivedFrom":[subQ1,subQ0]});Q121=makeQuery(id+"F0.imprint","IMPRINT",FACE,{"disambiguationData":[TD([[makeQuery(id+"F0.imprint","IMPRINT",EDGE,{"disambiguationData":[TD([[subQ2,-1.0]])],"derivedFrom":subQ1}),1.0]])]});}
            var Q122;
            {var subQ0=sQuery(id+"F0.wireOp",EDGE,"E29.left");var subQ1=sQuery(id+"F0.wireOp",EDGE,"E23");var subQ2=makeQuery(id+"F0.imprint","INTERSECT",VERTEX,{"disambiguationData":[OD(0.0)],"derivedFrom":[subQ1,subQ0]});Q122=makeQuery(id+"F0.imprint","IMPRINT",FACE,{"disambiguationData":[TD([[makeQuery(id+"F0.imprint","IMPRINT",EDGE,{"disambiguationData":[TD([[subQ2,-1.0]])],"derivedFrom":subQ1}),1.0]])]});}
            var Q123;
            {var subQ0=sQuery(id+"F0.wireOp",EDGE,"E29.left");var subQ1=sQuery(id+"F0.wireOp",EDGE,"E21");var subQ2=makeQuery(id+"F0.imprint","INTERSECT",VERTEX,{"disambiguationData":[OD(0.0)],"derivedFrom":[subQ1,subQ0]});Q123=makeQuery(id+"F0.imprint","IMPRINT",FACE,{"disambiguationData":[TD([[makeQuery(id+"F0.imprint","IMPRINT",EDGE,{"disambiguationData":[TD([[subQ2,-1.0]])],"derivedFrom":subQ1}),1.0]])]});}
            var Q124;
            {var subQ0=sQuery(id+"F0.wireOp",EDGE,"E29.left");var subQ1=sQuery(id+"F0.wireOp",EDGE,"E19");var subQ2=makeQuery(id+"F0.imprint","INTERSECT",VERTEX,{"disambiguationData":[OD(0.0)],"derivedFrom":[subQ1,subQ0]});Q124=makeQuery(id+"F0.imprint","IMPRINT",FACE,{"disambiguationData":[TD([[makeQuery(id+"F0.imprint","IMPRINT",EDGE,{"disambiguationData":[TD([[subQ2,-1.0]])],"derivedFrom":subQ1}),1.0]])]});}
            var Q125;
            {var subQ0=sQuery(id+"F0.wireOp",EDGE,"E29.left");var subQ1=sQuery(id+"F0.wireOp",EDGE,"E17");var subQ2=makeQuery(id+"F0.imprint","INTERSECT",VERTEX,{"disambiguationData":[OD(0.0)],"derivedFrom":[subQ1,subQ0]});Q125=makeQuery(id+"F0.imprint","IMPRINT",FACE,{"disambiguationData":[TD([[makeQuery(id+"F0.imprint","IMPRINT",EDGE,{"disambiguationData":[TD([[subQ2,-1.0]])],"derivedFrom":subQ1}),1.0]])]});}
            var Q126;
            {var subQ0=sQuery(id+"F0.wireOp",EDGE,"E29.left");var subQ1=sQuery(id+"F0.wireOp",EDGE,"E15");var subQ2=makeQuery(id+"F0.imprint","INTERSECT",VERTEX,{"disambiguationData":[OD(0.0)],"derivedFrom":[subQ1,subQ0]});Q126=makeQuery(id+"F0.imprint","IMPRINT",FACE,{"disambiguationData":[TD([[makeQuery(id+"F0.imprint","IMPRINT",EDGE,{"disambiguationData":[TD([[subQ2,-1.0]])],"derivedFrom":subQ1}),1.0]])]});}
            var Q127;
            {var subQ0=sQuery(id+"F0.wireOp",EDGE,"E29.left");var subQ1=sQuery(id+"F0.wireOp",EDGE,"E13");var subQ2=makeQuery(id+"F0.imprint","INTERSECT",VERTEX,{"disambiguationData":[OD(0.0)],"derivedFrom":[subQ1,subQ0]});Q127=makeQuery(id+"F0.imprint","IMPRINT",FACE,{"disambiguationData":[TD([[makeQuery(id+"F0.imprint","IMPRINT",EDGE,{"disambiguationData":[TD([[subQ2,-1.0]])],"derivedFrom":subQ1}),1.0]])]});}
            var Q128;
            {var subQ0=sQuery(id+"F0.wireOp",EDGE,"E29.left");var subQ1=sQuery(id+"F0.wireOp",EDGE,"E11");var subQ2=makeQuery(id+"F0.imprint","INTERSECT",VERTEX,{"disambiguationData":[OD(0.0)],"derivedFrom":[subQ1,subQ0]});Q128=makeQuery(id+"F0.imprint","IMPRINT",FACE,{"disambiguationData":[TD([[makeQuery(id+"F0.imprint","IMPRINT",EDGE,{"disambiguationData":[TD([[subQ2,-1.0]])],"derivedFrom":subQ1}),1.0]])]});}
            var Q129;
            {var subQ0=sQuery(id+"F0.wireOp",EDGE,"E29.left");var subQ1=sQuery(id+"F0.wireOp",EDGE,"E9");var subQ2=makeQuery(id+"F0.imprint","INTERSECT",VERTEX,{"disambiguationData":[OD(0.0)],"derivedFrom":[subQ1,subQ0]});Q129=makeQuery(id+"F0.imprint","IMPRINT",FACE,{"disambiguationData":[TD([[makeQuery(id+"F0.imprint","IMPRINT",EDGE,{"disambiguationData":[TD([[subQ2,-1.0]])],"derivedFrom":subQ1}),1.0]])]});}
            var Q130;
            {var subQ0=sQuery(id+"F0.wireOp",EDGE,"E29.left");var subQ1=sQuery(id+"F0.wireOp",EDGE,"E7");var subQ2=makeQuery(id+"F0.imprint","INTERSECT",VERTEX,{"disambiguationData":[OD(0.0)],"derivedFrom":[subQ1,subQ0]});Q130=makeQuery(id+"F0.imprint","IMPRINT",FACE,{"disambiguationData":[TD([[makeQuery(id+"F0.imprint","IMPRINT",EDGE,{"disambiguationData":[TD([[subQ2,-1.0]])],"derivedFrom":subQ1}),1.0]])]});}
            var Q131;
            {var subQ0=sQuery(id+"F0.wireOp",EDGE,"E29.left");var subQ1=sQuery(id+"F0.wireOp",EDGE,"E5");var subQ2=makeQuery(id+"F0.imprint","INTERSECT",VERTEX,{"disambiguationData":[OD(0.0)],"derivedFrom":[subQ1,subQ0]});Q131=makeQuery(id+"F0.imprint","IMPRINT",FACE,{"disambiguationData":[TD([[makeQuery(id+"F0.imprint","IMPRINT",EDGE,{"disambiguationData":[TD([[subQ2,-1.0]])],"derivedFrom":subQ1}),1.0]])]});}
            var Q132;
            {var subQ0=sQuery(id+"F0.wireOp",EDGE,"E29.left");var subQ1=sQuery(id+"F0.wireOp",EDGE,"E3");var subQ2=makeQuery(id+"F0.imprint","INTERSECT",VERTEX,{"disambiguationData":[OD(0.0)],"derivedFrom":[subQ1,subQ0]});Q132=makeQuery(id+"F0.imprint","IMPRINT",FACE,{"disambiguationData":[TD([[makeQuery(id+"F0.imprint","IMPRINT",EDGE,{"disambiguationData":[TD([[subQ2,-1.0]])],"derivedFrom":subQ1}),1.0]])]});}
            var Q133;
            {var subQ0=sQuery(id+"F0.wireOp",EDGE,"E29.right");var subQ1=sQuery(id+"F0.wireOp",EDGE,"E23");var subQ2=makeQuery(id+"F0.imprint","INTERSECT",VERTEX,{"disambiguationData":[OD(0.0)],"derivedFrom":[subQ1,subQ0]});Q133=makeQuery(id+"F0.imprint","IMPRINT",FACE,{"disambiguationData":[TD([[makeQuery(id+"F0.imprint","IMPRINT",EDGE,{"disambiguationData":[TD([[subQ2,1.0]])],"derivedFrom":subQ1}),1.0]])]});}
            var Q134;
            {var subQ0=sQuery(id+"F0.wireOp",EDGE,"E29.right");var subQ1=sQuery(id+"F0.wireOp",EDGE,"E21");var subQ2=makeQuery(id+"F0.imprint","INTERSECT",VERTEX,{"disambiguationData":[OD(0.0)],"derivedFrom":[subQ1,subQ0]});Q134=makeQuery(id+"F0.imprint","IMPRINT",FACE,{"disambiguationData":[TD([[makeQuery(id+"F0.imprint","IMPRINT",EDGE,{"disambiguationData":[TD([[subQ2,1.0]])],"derivedFrom":subQ1}),1.0]])]});}
            var Q135;
            {var subQ0=sQuery(id+"F0.wireOp",EDGE,"E29.right");var subQ1=sQuery(id+"F0.wireOp",EDGE,"E19");var subQ2=makeQuery(id+"F0.imprint","INTERSECT",VERTEX,{"disambiguationData":[OD(0.0)],"derivedFrom":[subQ1,subQ0]});Q135=makeQuery(id+"F0.imprint","IMPRINT",FACE,{"disambiguationData":[TD([[makeQuery(id+"F0.imprint","IMPRINT",EDGE,{"disambiguationData":[TD([[subQ2,1.0]])],"derivedFrom":subQ1}),1.0]])]});}
            var Q136;
            {var subQ0=sQuery(id+"F0.wireOp",EDGE,"E29.right");var subQ1=sQuery(id+"F0.wireOp",EDGE,"E17");var subQ2=makeQuery(id+"F0.imprint","INTERSECT",VERTEX,{"disambiguationData":[OD(0.0)],"derivedFrom":[subQ1,subQ0]});Q136=makeQuery(id+"F0.imprint","IMPRINT",FACE,{"disambiguationData":[TD([[makeQuery(id+"F0.imprint","IMPRINT",EDGE,{"disambiguationData":[TD([[subQ2,1.0]])],"derivedFrom":subQ1}),1.0]])]});}
            var Q137;
            {var subQ0=sQuery(id+"F0.wireOp",EDGE,"E29.right");var subQ1=sQuery(id+"F0.wireOp",EDGE,"E15");var subQ2=makeQuery(id+"F0.imprint","INTERSECT",VERTEX,{"disambiguationData":[OD(0.0)],"derivedFrom":[subQ1,subQ0]});Q137=makeQuery(id+"F0.imprint","IMPRINT",FACE,{"disambiguationData":[TD([[makeQuery(id+"F0.imprint","IMPRINT",EDGE,{"disambiguationData":[TD([[subQ2,1.0]])],"derivedFrom":subQ1}),1.0]])]});}
            var Q138;
            {var subQ0=sQuery(id+"F0.wireOp",EDGE,"E29.right");var subQ1=sQuery(id+"F0.wireOp",EDGE,"E13");var subQ2=makeQuery(id+"F0.imprint","INTERSECT",VERTEX,{"disambiguationData":[OD(0.0)],"derivedFrom":[subQ1,subQ0]});Q138=makeQuery(id+"F0.imprint","IMPRINT",FACE,{"disambiguationData":[TD([[makeQuery(id+"F0.imprint","IMPRINT",EDGE,{"disambiguationData":[TD([[subQ2,1.0]])],"derivedFrom":subQ1}),1.0]])]});}
            var Q139;
            {var subQ0=sQuery(id+"F0.wireOp",EDGE,"E29.right");var subQ1=sQuery(id+"F0.wireOp",EDGE,"E11");var subQ2=makeQuery(id+"F0.imprint","INTERSECT",VERTEX,{"disambiguationData":[OD(0.0)],"derivedFrom":[subQ1,subQ0]});Q139=makeQuery(id+"F0.imprint","IMPRINT",FACE,{"disambiguationData":[TD([[makeQuery(id+"F0.imprint","IMPRINT",EDGE,{"disambiguationData":[TD([[subQ2,1.0]])],"derivedFrom":subQ1}),1.0]])]});}
            var Q140;
            {var subQ0=sQuery(id+"F0.wireOp",EDGE,"E29.right");var subQ1=sQuery(id+"F0.wireOp",EDGE,"E9");var subQ2=makeQuery(id+"F0.imprint","INTERSECT",VERTEX,{"disambiguationData":[OD(0.0)],"derivedFrom":[subQ1,subQ0]});Q140=makeQuery(id+"F0.imprint","IMPRINT",FACE,{"disambiguationData":[TD([[makeQuery(id+"F0.imprint","IMPRINT",EDGE,{"disambiguationData":[TD([[subQ2,1.0]])],"derivedFrom":subQ1}),1.0]])]});}
            var Q141;
            {var subQ0=sQuery(id+"F0.wireOp",EDGE,"E29.right");var subQ1=sQuery(id+"F0.wireOp",EDGE,"E7");var subQ2=makeQuery(id+"F0.imprint","INTERSECT",VERTEX,{"disambiguationData":[OD(0.0)],"derivedFrom":[subQ1,subQ0]});Q141=makeQuery(id+"F0.imprint","IMPRINT",FACE,{"disambiguationData":[TD([[makeQuery(id+"F0.imprint","IMPRINT",EDGE,{"disambiguationData":[TD([[subQ2,1.0]])],"derivedFrom":subQ1}),1.0]])]});}
            var Q142;
            {var subQ0=sQuery(id+"F0.wireOp",EDGE,"E29.right");var subQ1=sQuery(id+"F0.wireOp",EDGE,"E5");var subQ2=makeQuery(id+"F0.imprint","INTERSECT",VERTEX,{"disambiguationData":[OD(0.0)],"derivedFrom":[subQ1,subQ0]});Q142=makeQuery(id+"F0.imprint","IMPRINT",FACE,{"disambiguationData":[TD([[makeQuery(id+"F0.imprint","IMPRINT",EDGE,{"disambiguationData":[TD([[subQ2,1.0]])],"derivedFrom":subQ1}),1.0]])]});}
            var Q143;
            {var subQ0=sQuery(id+"F0.wireOp",EDGE,"E29.right");var subQ1=sQuery(id+"F0.wireOp",EDGE,"E3");var subQ2=makeQuery(id+"F0.imprint","INTERSECT",VERTEX,{"disambiguationData":[OD(0.0)],"derivedFrom":[subQ1,subQ0]});Q143=makeQuery(id+"F0.imprint","IMPRINT",FACE,{"disambiguationData":[TD([[makeQuery(id+"F0.imprint","IMPRINT",EDGE,{"disambiguationData":[TD([[subQ2,1.0]])],"derivedFrom":subQ1}),1.0]])]});}
            var Q144;
            {var subQ0=sQuery(id+"F0.wireOp",EDGE,"E29.right");var subQ1=sQuery(id+"F0.wireOp",EDGE,"E23");var subQ2=makeQuery(id+"F0.imprint","INTERSECT",VERTEX,{"disambiguationData":[OD(1.0)],"derivedFrom":[subQ1,subQ0]});Q144=makeQuery(id+"F0.imprint","IMPRINT",FACE,{"disambiguationData":[TD([[makeQuery(id+"F0.imprint","IMPRINT",EDGE,{"disambiguationData":[TD([[subQ2,-1.0]])],"derivedFrom":subQ1}),1.0]])]});}
            var Q145;
            {var subQ0=sQuery(id+"F0.wireOp",EDGE,"E29.right");var subQ1=sQuery(id+"F0.wireOp",EDGE,"E21");var subQ2=makeQuery(id+"F0.imprint","INTERSECT",VERTEX,{"disambiguationData":[OD(1.0)],"derivedFrom":[subQ1,subQ0]});Q145=makeQuery(id+"F0.imprint","IMPRINT",FACE,{"disambiguationData":[TD([[makeQuery(id+"F0.imprint","IMPRINT",EDGE,{"disambiguationData":[TD([[subQ2,-1.0]])],"derivedFrom":subQ1}),1.0]])]});}
            var Q146;
            {var subQ0=sQuery(id+"F0.wireOp",EDGE,"E29.right");var subQ1=sQuery(id+"F0.wireOp",EDGE,"E19");var subQ2=makeQuery(id+"F0.imprint","INTERSECT",VERTEX,{"disambiguationData":[OD(1.0)],"derivedFrom":[subQ1,subQ0]});Q146=makeQuery(id+"F0.imprint","IMPRINT",FACE,{"disambiguationData":[TD([[makeQuery(id+"F0.imprint","IMPRINT",EDGE,{"disambiguationData":[TD([[subQ2,-1.0]])],"derivedFrom":subQ1}),1.0]])]});}
            var Q147;
            {var subQ0=sQuery(id+"F0.wireOp",EDGE,"E29.right");var subQ1=sQuery(id+"F0.wireOp",EDGE,"E17");var subQ2=makeQuery(id+"F0.imprint","INTERSECT",VERTEX,{"disambiguationData":[OD(1.0)],"derivedFrom":[subQ1,subQ0]});Q147=makeQuery(id+"F0.imprint","IMPRINT",FACE,{"disambiguationData":[TD([[makeQuery(id+"F0.imprint","IMPRINT",EDGE,{"disambiguationData":[TD([[subQ2,-1.0]])],"derivedFrom":subQ1}),1.0]])]});}
            var Q148;
            {var subQ0=sQuery(id+"F0.wireOp",EDGE,"E29.right");var subQ1=sQuery(id+"F0.wireOp",EDGE,"E15");var subQ2=makeQuery(id+"F0.imprint","INTERSECT",VERTEX,{"disambiguationData":[OD(1.0)],"derivedFrom":[subQ1,subQ0]});Q148=makeQuery(id+"F0.imprint","IMPRINT",FACE,{"disambiguationData":[TD([[makeQuery(id+"F0.imprint","IMPRINT",EDGE,{"disambiguationData":[TD([[subQ2,-1.0]])],"derivedFrom":subQ1}),1.0]])]});}
            var Q149;
            {var subQ0=sQuery(id+"F0.wireOp",EDGE,"E29.right");var subQ1=sQuery(id+"F0.wireOp",EDGE,"E13");var subQ2=makeQuery(id+"F0.imprint","INTERSECT",VERTEX,{"disambiguationData":[OD(1.0)],"derivedFrom":[subQ1,subQ0]});Q149=makeQuery(id+"F0.imprint","IMPRINT",FACE,{"disambiguationData":[TD([[makeQuery(id+"F0.imprint","IMPRINT",EDGE,{"disambiguationData":[TD([[subQ2,-1.0]])],"derivedFrom":subQ1}),1.0]])]});}
            var Q150;
            {var subQ0=sQuery(id+"F0.wireOp",EDGE,"E29.right");var subQ1=sQuery(id+"F0.wireOp",EDGE,"E11");var subQ2=makeQuery(id+"F0.imprint","INTERSECT",VERTEX,{"disambiguationData":[OD(1.0)],"derivedFrom":[subQ1,subQ0]});Q150=makeQuery(id+"F0.imprint","IMPRINT",FACE,{"disambiguationData":[TD([[makeQuery(id+"F0.imprint","IMPRINT",EDGE,{"disambiguationData":[TD([[subQ2,-1.0]])],"derivedFrom":subQ1}),1.0]])]});}
            var Q151;
            {var subQ0=sQuery(id+"F0.wireOp",EDGE,"E29.right");var subQ1=sQuery(id+"F0.wireOp",EDGE,"E9");var subQ2=makeQuery(id+"F0.imprint","INTERSECT",VERTEX,{"disambiguationData":[OD(1.0)],"derivedFrom":[subQ1,subQ0]});Q151=makeQuery(id+"F0.imprint","IMPRINT",FACE,{"disambiguationData":[TD([[makeQuery(id+"F0.imprint","IMPRINT",EDGE,{"disambiguationData":[TD([[subQ2,-1.0]])],"derivedFrom":subQ1}),1.0]])]});}
            var Q152;
            {var subQ0=sQuery(id+"F0.wireOp",EDGE,"E29.right");var subQ1=sQuery(id+"F0.wireOp",EDGE,"E7");var subQ2=makeQuery(id+"F0.imprint","INTERSECT",VERTEX,{"disambiguationData":[OD(1.0)],"derivedFrom":[subQ1,subQ0]});Q152=makeQuery(id+"F0.imprint","IMPRINT",FACE,{"disambiguationData":[TD([[makeQuery(id+"F0.imprint","IMPRINT",EDGE,{"disambiguationData":[TD([[subQ2,-1.0]])],"derivedFrom":subQ1}),1.0]])]});}
            var Q153;
            {var subQ0=sQuery(id+"F0.wireOp",EDGE,"E29.right");var subQ1=sQuery(id+"F0.wireOp",EDGE,"E5");var subQ2=makeQuery(id+"F0.imprint","INTERSECT",VERTEX,{"disambiguationData":[OD(1.0)],"derivedFrom":[subQ1,subQ0]});Q153=makeQuery(id+"F0.imprint","IMPRINT",FACE,{"disambiguationData":[TD([[makeQuery(id+"F0.imprint","IMPRINT",EDGE,{"disambiguationData":[TD([[subQ2,-1.0]])],"derivedFrom":subQ1}),1.0]])]});}
            var Q154;
            {var subQ0=sQuery(id+"F0.wireOp",EDGE,"E29.right");var subQ1=sQuery(id+"F0.wireOp",EDGE,"E3");var subQ2=makeQuery(id+"F0.imprint","INTERSECT",VERTEX,{"disambiguationData":[OD(1.0)],"derivedFrom":[subQ1,subQ0]});Q154=makeQuery(id+"F0.imprint","IMPRINT",FACE,{"disambiguationData":[TD([[makeQuery(id+"F0.imprint","IMPRINT",EDGE,{"disambiguationData":[TD([[subQ2,-1.0]])],"derivedFrom":subQ1}),1.0]])]});}
            var Q155;
            {var subQ0=sQuery(id+"F0.wireOp",EDGE,"E30.bottom");var subQ1=sQuery(id+"F0.wireOp",EDGE,"E23");var subQ2=makeQuery(id+"F0.imprint","INTERSECT",VERTEX,{"disambiguationData":[OD(0.0)],"derivedFrom":[subQ1,subQ0]});Q155=makeQuery(id+"F0.imprint","IMPRINT",FACE,{"disambiguationData":[TD([[makeQuery(id+"F0.imprint","IMPRINT",EDGE,{"disambiguationData":[TD([[subQ2,-1.0]])],"derivedFrom":subQ1}),1.0]])]});}
            var Q156;
            {var subQ0=sQuery(id+"F0.wireOp",EDGE,"E30.bottom");var subQ1=sQuery(id+"F0.wireOp",EDGE,"E21");var subQ2=makeQuery(id+"F0.imprint","INTERSECT",VERTEX,{"disambiguationData":[OD(0.0)],"derivedFrom":[subQ1,subQ0]});Q156=makeQuery(id+"F0.imprint","IMPRINT",FACE,{"disambiguationData":[TD([[makeQuery(id+"F0.imprint","IMPRINT",EDGE,{"disambiguationData":[TD([[subQ2,-1.0]])],"derivedFrom":subQ1}),1.0]])]});}
            var Q157;
            {var subQ0=sQuery(id+"F0.wireOp",EDGE,"E30.bottom");var subQ1=sQuery(id+"F0.wireOp",EDGE,"E19");var subQ2=makeQuery(id+"F0.imprint","INTERSECT",VERTEX,{"disambiguationData":[OD(0.0)],"derivedFrom":[subQ1,subQ0]});Q157=makeQuery(id+"F0.imprint","IMPRINT",FACE,{"disambiguationData":[TD([[makeQuery(id+"F0.imprint","IMPRINT",EDGE,{"disambiguationData":[TD([[subQ2,-1.0]])],"derivedFrom":subQ1}),1.0]])]});}
            var Q158;
            {var subQ0=sQuery(id+"F0.wireOp",EDGE,"E30.bottom");var subQ1=sQuery(id+"F0.wireOp",EDGE,"E17");var subQ2=makeQuery(id+"F0.imprint","INTERSECT",VERTEX,{"disambiguationData":[OD(0.0)],"derivedFrom":[subQ1,subQ0]});Q158=makeQuery(id+"F0.imprint","IMPRINT",FACE,{"disambiguationData":[TD([[makeQuery(id+"F0.imprint","IMPRINT",EDGE,{"disambiguationData":[TD([[subQ2,-1.0]])],"derivedFrom":subQ1}),1.0]])]});}
            var Q159;
            {var subQ0=sQuery(id+"F0.wireOp",EDGE,"E30.bottom");var subQ1=sQuery(id+"F0.wireOp",EDGE,"E15");var subQ2=makeQuery(id+"F0.imprint","INTERSECT",VERTEX,{"disambiguationData":[OD(0.0)],"derivedFrom":[subQ1,subQ0]});Q159=makeQuery(id+"F0.imprint","IMPRINT",FACE,{"disambiguationData":[TD([[makeQuery(id+"F0.imprint","IMPRINT",EDGE,{"disambiguationData":[TD([[subQ2,-1.0]])],"derivedFrom":subQ1}),1.0]])]});}
            var Q160;
            {var subQ0=sQuery(id+"F0.wireOp",EDGE,"E30.bottom");var subQ1=sQuery(id+"F0.wireOp",EDGE,"E13");var subQ2=makeQuery(id+"F0.imprint","INTERSECT",VERTEX,{"disambiguationData":[OD(0.0)],"derivedFrom":[subQ1,subQ0]});Q160=makeQuery(id+"F0.imprint","IMPRINT",FACE,{"disambiguationData":[TD([[makeQuery(id+"F0.imprint","IMPRINT",EDGE,{"disambiguationData":[TD([[subQ2,-1.0]])],"derivedFrom":subQ1}),1.0]])]});}
            var Q161;
            {var subQ0=sQuery(id+"F0.wireOp",EDGE,"E30.bottom");var subQ1=sQuery(id+"F0.wireOp",EDGE,"E11");var subQ2=makeQuery(id+"F0.imprint","INTERSECT",VERTEX,{"disambiguationData":[OD(0.0)],"derivedFrom":[subQ1,subQ0]});Q161=makeQuery(id+"F0.imprint","IMPRINT",FACE,{"disambiguationData":[TD([[makeQuery(id+"F0.imprint","IMPRINT",EDGE,{"disambiguationData":[TD([[subQ2,-1.0]])],"derivedFrom":subQ1}),1.0]])]});}
            var Q162;
            {var subQ0=sQuery(id+"F0.wireOp",EDGE,"E30.bottom");var subQ1=sQuery(id+"F0.wireOp",EDGE,"E9");var subQ2=makeQuery(id+"F0.imprint","INTERSECT",VERTEX,{"disambiguationData":[OD(0.0)],"derivedFrom":[subQ1,subQ0]});Q162=makeQuery(id+"F0.imprint","IMPRINT",FACE,{"disambiguationData":[TD([[makeQuery(id+"F0.imprint","IMPRINT",EDGE,{"disambiguationData":[TD([[subQ2,-1.0]])],"derivedFrom":subQ1}),1.0]])]});}
            var Q163;
            {var subQ0=sQuery(id+"F0.wireOp",EDGE,"E30.bottom");var subQ1=sQuery(id+"F0.wireOp",EDGE,"E7");var subQ2=makeQuery(id+"F0.imprint","INTERSECT",VERTEX,{"disambiguationData":[OD(0.0)],"derivedFrom":[subQ1,subQ0]});Q163=makeQuery(id+"F0.imprint","IMPRINT",FACE,{"disambiguationData":[TD([[makeQuery(id+"F0.imprint","IMPRINT",EDGE,{"disambiguationData":[TD([[subQ2,-1.0]])],"derivedFrom":subQ1}),1.0]])]});}
            var Q164;
            {var subQ0=sQuery(id+"F0.wireOp",EDGE,"E30.bottom");var subQ1=sQuery(id+"F0.wireOp",EDGE,"E5");var subQ2=makeQuery(id+"F0.imprint","INTERSECT",VERTEX,{"disambiguationData":[OD(0.0)],"derivedFrom":[subQ1,subQ0]});Q164=makeQuery(id+"F0.imprint","IMPRINT",FACE,{"disambiguationData":[TD([[makeQuery(id+"F0.imprint","IMPRINT",EDGE,{"disambiguationData":[TD([[subQ2,-1.0]])],"derivedFrom":subQ1}),1.0]])]});}
            var Q165;
            {var subQ0=sQuery(id+"F0.wireOp",EDGE,"E30.bottom");var subQ1=sQuery(id+"F0.wireOp",EDGE,"E3");var subQ2=makeQuery(id+"F0.imprint","INTERSECT",VERTEX,{"disambiguationData":[OD(0.0)],"derivedFrom":[subQ1,subQ0]});Q165=makeQuery(id+"F0.imprint","IMPRINT",FACE,{"disambiguationData":[TD([[makeQuery(id+"F0.imprint","IMPRINT",EDGE,{"disambiguationData":[TD([[subQ2,-1.0]])],"derivedFrom":subQ1}),1.0]])]});}
            var Q166;
            {var subQ0=sQuery(id+"F0.wireOp",EDGE,"E29.left");var subQ1=sQuery(id+"F0.wireOp",EDGE,"E1");var subQ2=makeQuery(id+"F0.imprint","INTERSECT",VERTEX,{"disambiguationData":[OD(0.0)],"derivedFrom":[subQ1,subQ0]});Q166=makeQuery(id+"F0.imprint","IMPRINT",FACE,{"disambiguationData":[TD([[makeQuery(id+"F0.imprint","IMPRINT",EDGE,{"disambiguationData":[TD([[subQ2,-1.0]])],"derivedFrom":subQ1}),1.0]])]});}
            var Q167;
            {var subQ0=sQuery(id+"F0.wireOp",EDGE,"E29.right");var subQ1=sQuery(id+"F0.wireOp",EDGE,"E1");var subQ2=makeQuery(id+"F0.imprint","INTERSECT",VERTEX,{"disambiguationData":[OD(0.0)],"derivedFrom":[subQ1,subQ0]});Q167=makeQuery(id+"F0.imprint","IMPRINT",FACE,{"disambiguationData":[TD([[makeQuery(id+"F0.imprint","IMPRINT",EDGE,{"disambiguationData":[TD([[subQ2,1.0]])],"derivedFrom":subQ1}),1.0]])]});}
            var Q168;
            {var subQ0=sQuery(id+"F0.wireOp",EDGE,"E29.right");var subQ1=sQuery(id+"F0.wireOp",EDGE,"E1");var subQ2=makeQuery(id+"F0.imprint","INTERSECT",VERTEX,{"disambiguationData":[OD(1.0)],"derivedFrom":[subQ1,subQ0]});Q168=makeQuery(id+"F0.imprint","IMPRINT",FACE,{"disambiguationData":[TD([[makeQuery(id+"F0.imprint","IMPRINT",EDGE,{"disambiguationData":[TD([[subQ2,-1.0]])],"derivedFrom":subQ1}),1.0]])]});}
            var Q169;
            {var subQ0=sQuery(id+"F0.wireOp",EDGE,"E30.bottom");var subQ1=sQuery(id+"F0.wireOp",EDGE,"E1");var subQ2=makeQuery(id+"F0.imprint","INTERSECT",VERTEX,{"disambiguationData":[OD(0.0)],"derivedFrom":[subQ1,subQ0]});Q169=makeQuery(id+"F0.imprint","IMPRINT",FACE,{"disambiguationData":[TD([[makeQuery(id+"F0.imprint","IMPRINT",EDGE,{"disambiguationData":[TD([[subQ2,-1.0]])],"derivedFrom":subQ1}),1.0]])]});}
            extrude(context, id + "F1", {"entities" : qUnion([Q0, Q1, Q2, Q3, Q4, Q5, Q6, Q7, Q8, Q9, Q10, Q11, Q12, Q13, Q14, Q15, Q16, Q17, Q18, Q19, Q20, Q21, Q22, Q23, Q24, Q25, Q26, Q27, Q28, Q29, Q30, Q31, Q32, Q33, Q34, Q35, Q36, Q37, Q38, Q39, Q40, Q41, Q42, Q43, Q44, Q45, Q46, Q47, Q48, Q49, Q50, Q51, Q52, Q53, Q54, Q55, Q56, Q57, Q58, Q59, Q60, Q61, Q62, Q63, Q64, Q65, Q66, Q67, Q68, Q69, Q70, Q71, Q72, Q73, Q74, Q75, Q76, Q77, Q78, Q79, Q80, Q81, Q82, Q83, Q84, Q85, Q86, Q87, Q88, Q89, Q90, Q91, Q92, Q93, Q94, Q95, Q96, Q97, Q98, Q99, Q100, Q101, Q102, Q103, Q104, Q105, Q106, Q107, Q108, Q109, Q110, Q111, Q112, Q113, Q114, Q115, Q116, Q117, Q118, Q119, Q120, Q121, Q122, Q123, Q124, Q125, Q126, Q127, Q128, Q129, Q130, Q131, Q132, Q133, Q134, Q135, Q136, Q137, Q138, Q139, Q140, Q141, Q142, Q143, Q144, Q145, Q146, Q147, Q148, Q149, Q150, Q151, Q152, Q153, Q154, Q155, Q156, Q157, Q158, Q159, Q160, Q161, Q162, Q163, Q164, Q165, Q166, Q167, Q168, Q169]), "depth" : 3 * mm, "offsetDistance" : 25 * mm});
        }
        {
            var Q0;
            {var subQ0=sQuery(id+"F0.wireOp",EDGE,"E30.bottom");var subQ1=sQuery(id+"F0.wireOp",EDGE,"E1");var subQ2=makeQuery(id+"F0.imprint","INTERSECT",VERTEX,{"disambiguationData":[OD(0.0)],"derivedFrom":[subQ1,subQ0]});Q0=makeQuery(id+"F0.imprint","IMPRINT",FACE,{"disambiguationData":[TD([[makeQuery(id+"F0.imprint","IMPRINT",EDGE,{"disambiguationData":[TD([[subQ2,-1.0]])],"derivedFrom":subQ1}),-1.0]])]});}
            var Q1;
            {var subQ0=sQuery(id+"F0.wireOp",EDGE,"E30.top");var subQ1=sQuery(id+"F0.wireOp",EDGE,"E1");var subQ2=makeQuery(id+"F0.imprint","INTERSECT",VERTEX,{"disambiguationData":[OD(1.0)],"derivedFrom":[subQ1,subQ0]});Q1=makeQuery(id+"F0.imprint","IMPRINT",FACE,{"disambiguationData":[TD([[makeQuery(id+"F0.imprint","IMPRINT",EDGE,{"disambiguationData":[TD([[subQ2,-1.0]])],"derivedFrom":subQ1}),-1.0]])]});}
            var Q2;
            {var subQ0=sQuery(id+"F0.wireOp",EDGE,"E29.left");var subQ1=sQuery(id+"F0.wireOp",EDGE,"E1");var subQ2=makeQuery(id+"F0.imprint","INTERSECT",VERTEX,{"disambiguationData":[OD(0.0)],"derivedFrom":[subQ1,subQ0]});Q2=makeQuery(id+"F0.imprint","IMPRINT",FACE,{"disambiguationData":[TD([[makeQuery(id+"F0.imprint","IMPRINT",EDGE,{"disambiguationData":[TD([[subQ2,-1.0]])],"derivedFrom":subQ1}),-1.0]])]});}
            var Q3;
            {var subQ0=sQuery(id+"F0.wireOp",EDGE,"E29.right");var subQ1=sQuery(id+"F0.wireOp",EDGE,"E1");var subQ2=makeQuery(id+"F0.imprint","INTERSECT",VERTEX,{"disambiguationData":[OD(0.0)],"derivedFrom":[subQ1,subQ0]});Q3=makeQuery(id+"F0.imprint","IMPRINT",FACE,{"disambiguationData":[TD([[makeQuery(id+"F0.imprint","IMPRINT",EDGE,{"disambiguationData":[TD([[subQ2,-1.0]])],"derivedFrom":subQ1}),-1.0]])]});}
            var Q4;
            {var subQ0=sQuery(id+"F0.wireOp",EDGE,"E29.right");var subQ1=sQuery(id+"F0.wireOp",EDGE,"E1");var subQ2=makeQuery(id+"F0.imprint","INTERSECT",VERTEX,{"disambiguationData":[OD(0.0)],"derivedFrom":[subQ1,subQ0]});Q4=makeQuery(id+"F0.imprint","IMPRINT",FACE,{"disambiguationData":[TD([[makeQuery(id+"F0.imprint","IMPRINT",EDGE,{"disambiguationData":[TD([[subQ2,1.0]])],"derivedFrom":subQ1}),-1.0]])]});}
            var Q5;
            {var subQ0=sQuery(id+"F0.wireOp",EDGE,"E30.top");var subQ1=sQuery(id+"F0.wireOp",EDGE,"E1");var subQ2=makeQuery(id+"F0.imprint","INTERSECT",VERTEX,{"disambiguationData":[OD(0.0)],"derivedFrom":[subQ1,subQ0]});Q5=makeQuery(id+"F0.imprint","IMPRINT",FACE,{"disambiguationData":[TD([[makeQuery(id+"F0.imprint","IMPRINT",EDGE,{"disambiguationData":[TD([[subQ2,1.0]])],"derivedFrom":subQ1}),-1.0]])]});}
            var Q6;
            {var subQ0=sQuery(id+"F0.wireOp",EDGE,"E29.right");var subQ1=sQuery(id+"F0.wireOp",EDGE,"E1");var subQ2=makeQuery(id+"F0.imprint","INTERSECT",VERTEX,{"disambiguationData":[OD(1.0)],"derivedFrom":[subQ1,subQ0]});Q6=makeQuery(id+"F0.imprint","IMPRINT",FACE,{"disambiguationData":[TD([[makeQuery(id+"F0.imprint","IMPRINT",EDGE,{"disambiguationData":[TD([[subQ2,-1.0]])],"derivedFrom":subQ1}),-1.0]])]});}
            var Q7;
            {var subQ0=sQuery(id+"F0.wireOp",EDGE,"E29.left");var subQ1=sQuery(id+"F0.wireOp",EDGE,"E1");var subQ2=makeQuery(id+"F0.imprint","INTERSECT",VERTEX,{"disambiguationData":[OD(1.0)],"derivedFrom":[subQ1,subQ0]});Q7=makeQuery(id+"F0.imprint","IMPRINT",FACE,{"disambiguationData":[TD([[makeQuery(id+"F0.imprint","IMPRINT",EDGE,{"disambiguationData":[TD([[subQ2,-1.0]])],"derivedFrom":subQ1}),-1.0]])]});}
            extrude(context, id + "F2", {"entities" : qUnion([Q0, Q1, Q2, Q3, Q4, Q5, Q6, Q7]), "operationType" : NewBodyOperationType.ADD, "depth" : 1 * mm, "offsetDistance" : 25 * mm});
        }
    });
